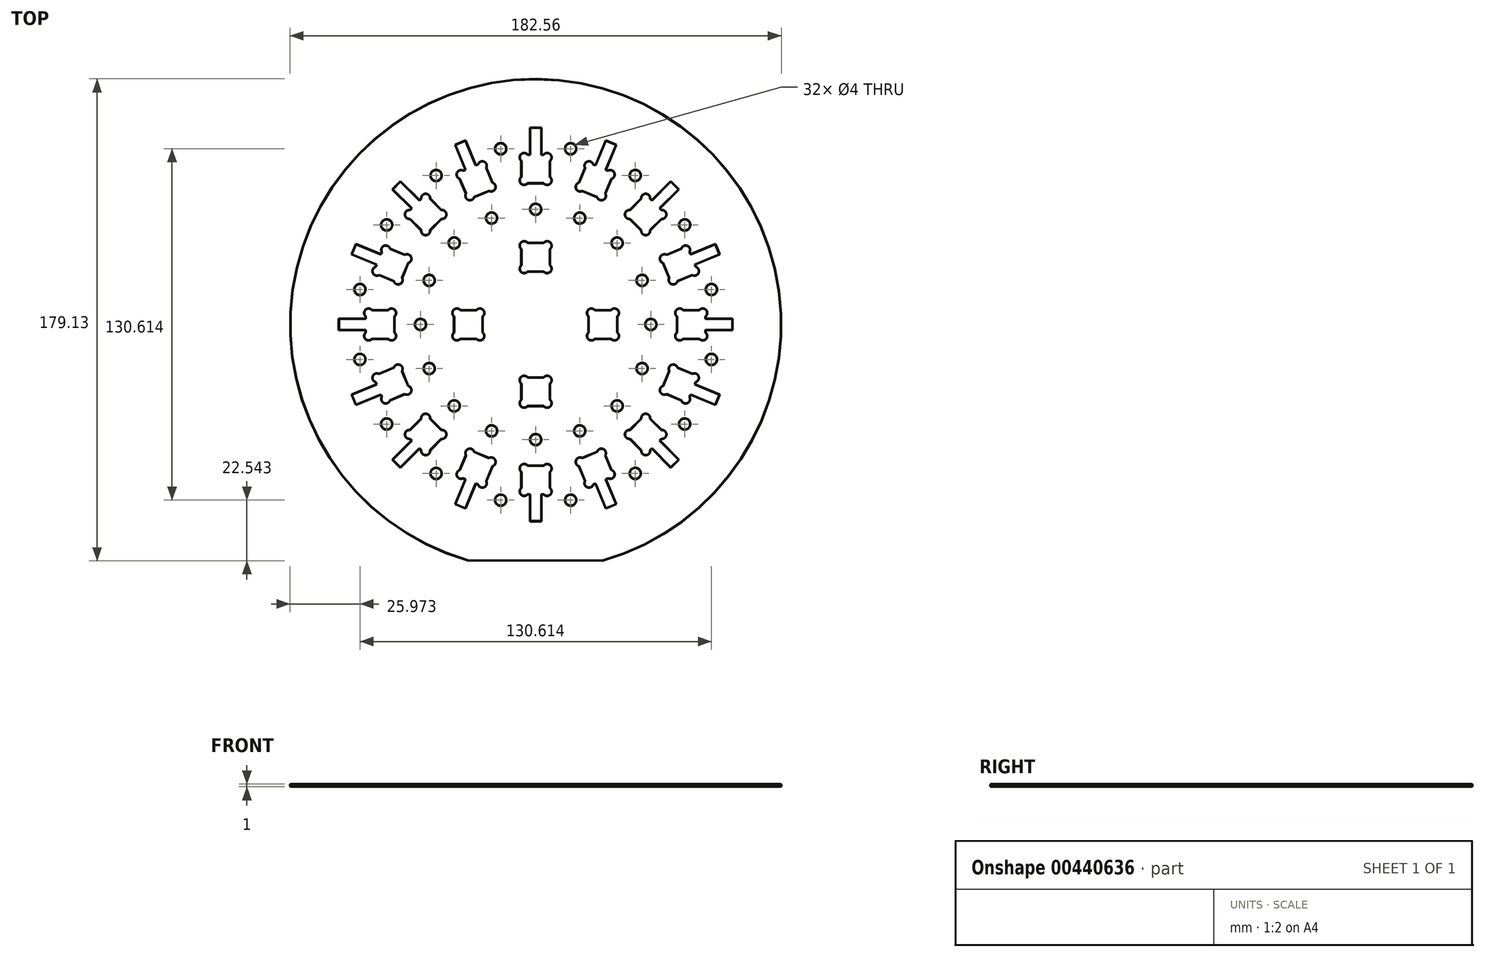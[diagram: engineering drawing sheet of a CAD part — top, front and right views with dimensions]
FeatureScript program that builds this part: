
annotation { "Feature Type Name" : "Feature", "Feature Type Description" : "" }
export const myFeature = defineFeature(function(context is Context, id is Id, definition is map)
    precondition{}
    {
        {
            var Q0;
            Q0=qCreatedBy(makeId("Top.planeOp"),FACE);
            var sketch = newSketch(context, id + "F0", { "sketchPlane" : qUnion([Q0])});
            skArc(sketch, "E0", {"start": v(24.78, -87.85) * mm, "mid": v(0.23, 91.28) * mm, "end": v(-25.22, -87.73) * mm});
            skLineSegment(sketch, "E1", {"start": v(-25.22, -87.73) * mm, "end": v(24.78, -87.85) * mm});
            skLineSegment(sketch, "E2", {"start": v(0, 0) * mm, "end": v(-0.22, -87.8) * mm, "construction": true});
            skLineSegment(sketch, "E3.bottom", {"start": v(5.25, 52.56) * mm, "end": v(3.02, 52.56) * mm, "construction": true});
            skLineSegment(sketch, "E3.top", {"start": v(5.25, 63.06) * mm, "end": v(3.02, 63.06) * mm, "construction": true});
            skLineSegment(sketch, "E3.left", {"start": v(5.25, 52.56) * mm, "end": v(5.25, 52.56) * mm});
            skLineSegment(sketch, "E3.right", {"start": v(-5.25, 52.56) * mm, "end": v(-5.25, 54.79) * mm, "construction": true});
            skPoint(sketch, "E3.middle", {"position": v(0, 57.8) * mm});
            skLineSegment(sketch, "E4", {"start": v(0, 57.8) * mm, "end": v(5.25, 63.06) * mm, "construction": true});
            skLineSegment(sketch, "E5", {"start": v(5.25, 63.06) * mm, "end": v(5.4, 63.2) * mm, "construction": true});
            skArc(sketch, "E6", {"start": v(5.25, 60.83) * mm, "mid": v(5.4, 63.2) * mm, "end": v(3.02, 63.06) * mm});
            skArc(sketch, "E7", {"start": v(3.02, 63.06) * mm, "mid": v(3.15, 60.95) * mm, "end": v(5.25, 60.83) * mm, "construction": true});
            skLineSegment(sketch, "E8", {"start": v(5.25, 60.83) * mm, "end": v(5.25, 63.06) * mm, "construction": true});
            skLineSegment(sketch, "E9", {"start": v(5.25, 52.56) * mm, "end": v(5.25, 54.79) * mm, "construction": true});
            skLineSegment(sketch, "E10", {"start": v(3.02, 63.06) * mm, "end": v(3.02, 63.06) * mm});
            skLineSegment(sketch, "E11", {"start": v(-5.25, 63.06) * mm, "end": v(-5.25, 63.06) * mm});
            skArc(sketch, "E12.1.0", {"start": v(-3.02, 63.06) * mm, "mid": v(-5.4, 63.2) * mm, "end": v(-5.25, 60.83) * mm});
            skArc(sketch, "E12.2.0", {"start": v(-5.25, 54.79) * mm, "mid": v(-5.4, 52.42) * mm, "end": v(-3.02, 52.56) * mm});
            skArc(sketch, "E13.2.3.0", {"start": v(3.02, 52.56) * mm, "mid": v(5.4, 52.42) * mm, "end": v(5.25, 54.79) * mm});
            skLineSegment(sketch, "E14", {"start": v(-5.25, 60.83) * mm, "end": v(-5.25, 63.06) * mm, "construction": true});
            skLineSegment(sketch, "E15", {"start": v(-5.25, 54.79) * mm, "end": v(-5.25, 60.83) * mm});
            skLineSegment(sketch, "E16", {"start": v(-3.02, 52.56) * mm, "end": v(-5.25, 52.56) * mm, "construction": true});
            skLineSegment(sketch, "E17", {"start": v(3.02, 52.56) * mm, "end": v(-3.02, 52.56) * mm});
            skLineSegment(sketch, "E18", {"start": v(3.02, 63.06) * mm, "end": v(-3.02, 63.06) * mm});
            skLineSegment(sketch, "E19", {"start": v(-3.02, 63.06) * mm, "end": v(-5.25, 63.06) * mm, "construction": true});
            skLineSegment(sketch, "E20", {"start": v(5.25, 54.79) * mm, "end": v(5.25, 60.83) * mm});
            skLineSegment(sketch, "E21", {"start": v(5.25, 60.83) * mm, "end": v(5.25, 60.83) * mm});
            skLineSegment(sketch, "E22", {"start": v(0, 57.8) * mm, "end": v(0, 42.8) * mm, "construction": true});
            skCircle(sketch, "E23", {"center": v(0, 42.8) * mm, "radius": 2 * mm});
            skCircle(sketch, "E24.1.0", {"center": v(13, 65.3) * mm, "radius": 2 * mm});
            skCircle(sketch, "E24.2.0", {"center": v(-13, 65.3) * mm, "radius": 2 * mm});
            skLineSegment(sketch, "E25.1.0", {"start": v(-25.82, 48.6) * mm, "end": v(-28.13, 54.19) * mm});
            skLineSegment(sketch, "E25.1.1", {"start": v(-17.32, 49.71) * mm, "end": v(-22.9, 47.4) * mm});
            skCircle(sketch, "E25.1.2", {"center": v(-16.38, 39.55) * mm, "radius": 2 * mm});
            skLineSegment(sketch, "E25.1.3", {"start": v(-22.12, 53.4) * mm, "end": v(-16.38, 39.55) * mm, "construction": true});
            skCircle(sketch, "E25.1.4", {"center": v(-37, 55.36) * mm, "radius": 2 * mm});
            skLineSegment(sketch, "E25.1.6", {"start": v(-16.12, 52.62) * mm, "end": v(-18.43, 58.2) * mm});
            skArc(sketch, "E25.1.7", {"start": v(-21.34, 59.41) * mm, "mid": v(-20.42, 57.52) * mm, "end": v(-18.43, 58.2) * mm, "construction": true});
            skPoint(sketch, "E25.1.8", {"position": v(-22.12, 53.4) * mm});
            skLineSegment(sketch, "E25.1.9", {"start": v(-22.12, 53.4) * mm, "end": v(-19.28, 60.27) * mm, "construction": true});
            skLineSegment(sketch, "E25.1.10", {"start": v(-21.34, 59.41) * mm, "end": v(-26.92, 57.1) * mm});
            skPoint(sketch, "E25.1.11", {"position": v(-22.12, 53.4) * mm});
            skArc(sketch, "E25.1.12", {"start": v(-25.82, 48.6) * mm, "mid": v(-25.04, 46.36) * mm, "end": v(-22.9, 47.4) * mm});
            skPoint(sketch, "E25.1.13", {"position": v(-22.12, 53.4) * mm});
            skLineSegment(sketch, "E25.1.14", {"start": v(-24.96, 46.55) * mm, "end": v(-25.82, 48.6) * mm, "construction": true});
            skLineSegment(sketch, "E25.1.15", {"start": v(-26.92, 57.1) * mm, "end": v(-28.98, 56.25) * mm, "construction": true});
            skArc(sketch, "E25.1.16", {"start": v(-26.92, 57.1) * mm, "mid": v(-29.17, 56.32) * mm, "end": v(-28.13, 54.19) * mm});
            skLineSegment(sketch, "E25.1.17", {"start": v(-15.26, 50.57) * mm, "end": v(-16.12, 52.62) * mm, "construction": true});
            skPoint(sketch, "E25.1.18", {"position": v(-22.12, 53.4) * mm});
            skLineSegment(sketch, "E25.1.19", {"start": v(-22.9, 47.4) * mm, "end": v(-24.96, 46.55) * mm, "construction": true});
            skArc(sketch, "E25.1.20", {"start": v(-17.32, 49.71) * mm, "mid": v(-15.08, 50.49) * mm, "end": v(-16.12, 52.62) * mm});
            skLineSegment(sketch, "E25.1.21", {"start": v(-15.26, 50.57) * mm, "end": v(-17.32, 49.71) * mm, "construction": true});
            skLineSegment(sketch, "E25.1.22", {"start": v(-28.13, 54.19) * mm, "end": v(-28.98, 56.25) * mm, "construction": true});
            skPoint(sketch, "E25.1.23", {"position": v(-22.12, 53.4) * mm});
            skPoint(sketch, "E25.1.24", {"position": v(-22.12, 53.4) * mm});
            skLineSegment(sketch, "E25.1.25", {"start": v(-18.43, 58.2) * mm, "end": v(-19.28, 60.27) * mm, "construction": true});
            skArc(sketch, "E25.1.26", {"start": v(-18.43, 58.2) * mm, "mid": v(-19.2, 60.45) * mm, "end": v(-21.34, 59.41) * mm});
            skLineSegment(sketch, "E25.1.27", {"start": v(-19.28, 60.27) * mm, "end": v(-19.2, 60.45) * mm, "construction": true});
            skLineSegment(sketch, "E25.1.28", {"start": v(-19.28, 60.27) * mm, "end": v(-21.34, 59.41) * mm, "construction": true});
            skLineSegment(sketch, "E25.2.0", {"start": v(-42.45, 35.03) * mm, "end": v(-46.72, 39.3) * mm});
            skLineSegment(sketch, "E25.2.1", {"start": v(-35.03, 39.3) * mm, "end": v(-39.3, 35.03) * mm});
            skCircle(sketch, "E25.2.2", {"center": v(-30.27, 30.27) * mm, "radius": 2 * mm});
            skLineSegment(sketch, "E25.2.3", {"start": v(-40.88, 40.88) * mm, "end": v(-30.27, 30.27) * mm, "construction": true});
            skCircle(sketch, "E25.2.4", {"center": v(-55.36, 37) * mm, "radius": 2 * mm});
            skCircle(sketch, "E25.2.5", {"center": v(-37, 55.36) * mm, "radius": 2 * mm});
            skLineSegment(sketch, "E25.2.6", {"start": v(-35.03, 42.45) * mm, "end": v(-39.3, 46.72) * mm});
            skArc(sketch, "E25.2.7", {"start": v(-42.45, 46.72) * mm, "mid": v(-40.88, 45.33) * mm, "end": v(-39.3, 46.72) * mm, "construction": true});
            skPoint(sketch, "E25.2.8", {"position": v(-40.88, 40.88) * mm});
            skLineSegment(sketch, "E25.2.9", {"start": v(-40.88, 40.88) * mm, "end": v(-40.88, 48.3) * mm, "construction": true});
            skLineSegment(sketch, "E25.2.10", {"start": v(-42.45, 46.72) * mm, "end": v(-46.72, 42.45) * mm});
            skPoint(sketch, "E25.2.11", {"position": v(-40.88, 40.88) * mm});
            skArc(sketch, "E25.2.12", {"start": v(-42.45, 35.03) * mm, "mid": v(-40.88, 33.25) * mm, "end": v(-39.3, 35.03) * mm});
            skPoint(sketch, "E25.2.13", {"position": v(-40.88, 40.88) * mm});
            skLineSegment(sketch, "E25.2.14", {"start": v(-40.88, 33.45) * mm, "end": v(-42.45, 35.03) * mm, "construction": true});
            skLineSegment(sketch, "E25.2.15", {"start": v(-46.72, 42.45) * mm, "end": v(-48.3, 40.88) * mm, "construction": true});
            skArc(sketch, "E25.2.16", {"start": v(-46.72, 42.45) * mm, "mid": v(-48.5, 40.88) * mm, "end": v(-46.72, 39.3) * mm});
            skLineSegment(sketch, "E25.2.17", {"start": v(-33.45, 40.88) * mm, "end": v(-35.03, 42.45) * mm, "construction": true});
            skPoint(sketch, "E25.2.18", {"position": v(-40.88, 40.88) * mm});
            skLineSegment(sketch, "E25.2.19", {"start": v(-39.3, 35.03) * mm, "end": v(-40.88, 33.45) * mm, "construction": true});
            skArc(sketch, "E25.2.20", {"start": v(-35.03, 39.3) * mm, "mid": v(-33.25, 40.88) * mm, "end": v(-35.03, 42.45) * mm});
            skLineSegment(sketch, "E25.2.21", {"start": v(-33.45, 40.88) * mm, "end": v(-35.03, 39.3) * mm, "construction": true});
            skLineSegment(sketch, "E25.2.22", {"start": v(-46.72, 39.3) * mm, "end": v(-48.3, 40.88) * mm, "construction": true});
            skPoint(sketch, "E25.2.23", {"position": v(-40.88, 40.88) * mm});
            skPoint(sketch, "E25.2.24", {"position": v(-40.88, 40.88) * mm});
            skLineSegment(sketch, "E25.2.25", {"start": v(-39.3, 46.72) * mm, "end": v(-40.88, 48.3) * mm, "construction": true});
            skArc(sketch, "E25.2.26", {"start": v(-39.3, 46.72) * mm, "mid": v(-40.88, 48.5) * mm, "end": v(-42.45, 46.72) * mm});
            skLineSegment(sketch, "E25.2.27", {"start": v(-40.88, 48.3) * mm, "end": v(-40.88, 48.5) * mm, "construction": true});
            skLineSegment(sketch, "E25.2.28", {"start": v(-40.88, 48.3) * mm, "end": v(-42.45, 46.72) * mm, "construction": true});
            skLineSegment(sketch, "E26.3.3.0", {"start": v(-47.4, 22.9) * mm, "end": v(-49.71, 17.32) * mm});
            skCircle(sketch, "E26.6.3.0", {"center": v(-39.55, 16.38) * mm, "radius": 2 * mm});
            skLineSegment(sketch, "E26.7.3.0", {"start": v(-52.62, 16.12) * mm, "end": v(-58.2, 18.43) * mm});
            skLineSegment(sketch, "E26.8.3.0", {"start": v(-53.4, 22.12) * mm, "end": v(-39.55, 16.38) * mm, "construction": true});
            skCircle(sketch, "E26.11.3.0", {"center": v(-65.3, 13) * mm, "radius": 2 * mm});
            skLineSegment(sketch, "E26.15.3.0", {"start": v(-48.6, 25.82) * mm, "end": v(-54.19, 28.13) * mm});
            skArc(sketch, "E26.18.3.0", {"start": v(-57.1, 26.92) * mm, "mid": v(-55.1, 26.23) * mm, "end": v(-54.19, 28.13) * mm, "construction": true});
            skPoint(sketch, "E26.22.3.0", {"position": v(-53.4, 22.12) * mm});
            skLineSegment(sketch, "E26.23.3.0", {"start": v(-53.4, 22.12) * mm, "end": v(-56.25, 28.98) * mm, "construction": true});
            skLineSegment(sketch, "E26.26.3.0", {"start": v(-57.1, 26.92) * mm, "end": v(-59.41, 21.34) * mm});
            skPoint(sketch, "E26.29.3.0", {"position": v(-53.4, 22.12) * mm});
            skArc(sketch, "E26.30.3.0", {"start": v(-52.62, 16.12) * mm, "mid": v(-50.49, 15.08) * mm, "end": v(-49.71, 17.32) * mm});
            skPoint(sketch, "E26.34.3.0", {"position": v(-53.4, 22.12) * mm});
            skLineSegment(sketch, "E26.35.3.0", {"start": v(-50.57, 15.26) * mm, "end": v(-52.62, 16.12) * mm, "construction": true});
            skLineSegment(sketch, "E26.38.3.0", {"start": v(-59.41, 21.34) * mm, "end": v(-60.27, 19.28) * mm, "construction": true});
            skArc(sketch, "E26.41.3.0", {"start": v(-59.41, 21.34) * mm, "mid": v(-60.45, 19.2) * mm, "end": v(-58.2, 18.43) * mm});
            skLineSegment(sketch, "E26.45.3.0", {"start": v(-46.55, 24.96) * mm, "end": v(-48.6, 25.82) * mm, "construction": true});
            skPoint(sketch, "E26.48.3.0", {"position": v(-53.4, 22.12) * mm});
            skLineSegment(sketch, "E26.49.3.0", {"start": v(-49.71, 17.32) * mm, "end": v(-50.57, 15.26) * mm, "construction": true});
            skArc(sketch, "E26.52.3.0", {"start": v(-47.4, 22.9) * mm, "mid": v(-46.36, 25.04) * mm, "end": v(-48.6, 25.82) * mm});
            skLineSegment(sketch, "E26.56.3.0", {"start": v(-46.55, 24.96) * mm, "end": v(-47.4, 22.9) * mm, "construction": true});
            skLineSegment(sketch, "E26.59.3.0", {"start": v(-58.2, 18.43) * mm, "end": v(-60.27, 19.28) * mm, "construction": true});
            skPoint(sketch, "E26.62.3.0", {"position": v(-53.4, 22.12) * mm});
            skPoint(sketch, "E26.63.3.0", {"position": v(-53.4, 22.12) * mm});
            skLineSegment(sketch, "E26.64.3.0", {"start": v(-54.19, 28.13) * mm, "end": v(-56.25, 28.98) * mm, "construction": true});
            skArc(sketch, "E26.67.3.0", {"start": v(-54.19, 28.13) * mm, "mid": v(-56.32, 29.17) * mm, "end": v(-57.1, 26.92) * mm});
            skLineSegment(sketch, "E26.71.3.0", {"start": v(-56.25, 28.98) * mm, "end": v(-56.32, 29.17) * mm, "construction": true});
            skLineSegment(sketch, "E26.74.3.0", {"start": v(-56.25, 28.98) * mm, "end": v(-57.1, 26.92) * mm, "construction": true});
            skLineSegment(sketch, "E26.3.4.0", {"start": v(-52.56, 3.02) * mm, "end": v(-52.56, -3.02) * mm});
            skCircle(sketch, "E26.6.4.0", {"center": v(-42.8, 0) * mm, "radius": 2 * mm});
            skLineSegment(sketch, "E26.7.4.0", {"start": v(-54.79, -5.25) * mm, "end": v(-60.83, -5.25) * mm});
            skLineSegment(sketch, "E26.8.4.0", {"start": v(-57.8, 0) * mm, "end": v(-42.8, 0) * mm, "construction": true});
            skCircle(sketch, "E26.11.4.0", {"center": v(-65.3, -13) * mm, "radius": 2 * mm});
            skCircle(sketch, "E26.13.4.0", {"center": v(-65.3, 13) * mm, "radius": 2 * mm});
            skLineSegment(sketch, "E26.15.4.0", {"start": v(-54.79, 5.25) * mm, "end": v(-60.83, 5.25) * mm});
            skArc(sketch, "E26.18.4.0", {"start": v(-63.06, 3.02) * mm, "mid": v(-60.95, 3.15) * mm, "end": v(-60.83, 5.25) * mm, "construction": true});
            skPoint(sketch, "E26.22.4.0", {"position": v(-57.8, 0) * mm});
            skLineSegment(sketch, "E26.23.4.0", {"start": v(-57.8, 0) * mm, "end": v(-63.06, 5.25) * mm, "construction": true});
            skLineSegment(sketch, "E26.26.4.0", {"start": v(-63.06, 3.02) * mm, "end": v(-63.06, -3.02) * mm});
            skPoint(sketch, "E26.29.4.0", {"position": v(-57.8, 0) * mm});
            skArc(sketch, "E26.30.4.0", {"start": v(-54.79, -5.25) * mm, "mid": v(-52.42, -5.4) * mm, "end": v(-52.56, -3.02) * mm});
            skPoint(sketch, "E26.34.4.0", {"position": v(-57.8, 0) * mm});
            skLineSegment(sketch, "E26.35.4.0", {"start": v(-52.56, -5.25) * mm, "end": v(-54.79, -5.25) * mm, "construction": true});
            skLineSegment(sketch, "E26.38.4.0", {"start": v(-63.06, -3.02) * mm, "end": v(-63.06, -5.25) * mm, "construction": true});
            skArc(sketch, "E26.41.4.0", {"start": v(-63.06, -3.02) * mm, "mid": v(-63.2, -5.4) * mm, "end": v(-60.83, -5.25) * mm});
            skLineSegment(sketch, "E26.45.4.0", {"start": v(-52.56, 5.25) * mm, "end": v(-54.79, 5.25) * mm, "construction": true});
            skPoint(sketch, "E26.48.4.0", {"position": v(-57.8, 0) * mm});
            skLineSegment(sketch, "E26.49.4.0", {"start": v(-52.56, -3.02) * mm, "end": v(-52.56, -5.25) * mm, "construction": true});
            skArc(sketch, "E26.52.4.0", {"start": v(-52.56, 3.02) * mm, "mid": v(-52.42, 5.4) * mm, "end": v(-54.79, 5.25) * mm});
            skLineSegment(sketch, "E26.56.4.0", {"start": v(-52.56, 5.25) * mm, "end": v(-52.56, 3.02) * mm, "construction": true});
            skLineSegment(sketch, "E26.59.4.0", {"start": v(-60.83, -5.25) * mm, "end": v(-63.06, -5.25) * mm, "construction": true});
            skPoint(sketch, "E26.62.4.0", {"position": v(-57.8, 0) * mm});
            skPoint(sketch, "E26.63.4.0", {"position": v(-57.8, 0) * mm});
            skLineSegment(sketch, "E26.64.4.0", {"start": v(-60.83, 5.25) * mm, "end": v(-63.06, 5.25) * mm, "construction": true});
            skArc(sketch, "E26.67.4.0", {"start": v(-60.83, 5.25) * mm, "mid": v(-63.2, 5.4) * mm, "end": v(-63.06, 3.02) * mm});
            skLineSegment(sketch, "E26.71.4.0", {"start": v(-63.06, 5.25) * mm, "end": v(-63.2, 5.4) * mm, "construction": true});
            skLineSegment(sketch, "E26.74.4.0", {"start": v(-63.06, 5.25) * mm, "end": v(-63.06, 3.02) * mm, "construction": true});
            skLineSegment(sketch, "E27.3.5.0", {"start": v(-49.71, -17.32) * mm, "end": v(-47.4, -22.9) * mm});
            skCircle(sketch, "E27.6.5.0", {"center": v(-39.55, -16.38) * mm, "radius": 2 * mm});
            skLineSegment(sketch, "E27.7.5.0", {"start": v(-48.6, -25.82) * mm, "end": v(-54.19, -28.13) * mm});
            skLineSegment(sketch, "E27.8.5.0", {"start": v(-53.4, -22.12) * mm, "end": v(-39.55, -16.38) * mm, "construction": true});
            skCircle(sketch, "E27.11.5.0", {"center": v(-55.36, -37) * mm, "radius": 2 * mm});
            skLineSegment(sketch, "E27.15.5.0", {"start": v(-52.62, -16.12) * mm, "end": v(-58.2, -18.43) * mm});
            skArc(sketch, "E27.18.5.0", {"start": v(-59.41, -21.34) * mm, "mid": v(-57.52, -20.42) * mm, "end": v(-58.2, -18.43) * mm, "construction": true});
            skPoint(sketch, "E27.22.5.0", {"position": v(-53.4, -22.12) * mm});
            skLineSegment(sketch, "E27.23.5.0", {"start": v(-53.4, -22.12) * mm, "end": v(-60.27, -19.28) * mm, "construction": true});
            skLineSegment(sketch, "E27.26.5.0", {"start": v(-59.41, -21.34) * mm, "end": v(-57.1, -26.92) * mm});
            skPoint(sketch, "E27.29.5.0", {"position": v(-53.4, -22.12) * mm});
            skArc(sketch, "E27.30.5.0", {"start": v(-48.6, -25.82) * mm, "mid": v(-46.36, -25.04) * mm, "end": v(-47.4, -22.9) * mm});
            skPoint(sketch, "E27.34.5.0", {"position": v(-53.4, -22.12) * mm});
            skLineSegment(sketch, "E27.35.5.0", {"start": v(-46.55, -24.96) * mm, "end": v(-48.6, -25.82) * mm, "construction": true});
            skLineSegment(sketch, "E27.38.5.0", {"start": v(-57.1, -26.92) * mm, "end": v(-56.25, -28.98) * mm, "construction": true});
            skArc(sketch, "E27.41.5.0", {"start": v(-57.1, -26.92) * mm, "mid": v(-56.32, -29.17) * mm, "end": v(-54.19, -28.13) * mm});
            skLineSegment(sketch, "E27.45.5.0", {"start": v(-50.57, -15.26) * mm, "end": v(-52.62, -16.12) * mm, "construction": true});
            skPoint(sketch, "E27.48.5.0", {"position": v(-53.4, -22.12) * mm});
            skLineSegment(sketch, "E27.49.5.0", {"start": v(-47.4, -22.9) * mm, "end": v(-46.55, -24.96) * mm, "construction": true});
            skArc(sketch, "E27.52.5.0", {"start": v(-49.71, -17.32) * mm, "mid": v(-50.49, -15.08) * mm, "end": v(-52.62, -16.12) * mm});
            skLineSegment(sketch, "E27.56.5.0", {"start": v(-50.57, -15.26) * mm, "end": v(-49.71, -17.32) * mm, "construction": true});
            skLineSegment(sketch, "E27.59.5.0", {"start": v(-54.19, -28.13) * mm, "end": v(-56.25, -28.98) * mm, "construction": true});
            skPoint(sketch, "E27.62.5.0", {"position": v(-53.4, -22.12) * mm});
            skPoint(sketch, "E27.63.5.0", {"position": v(-53.4, -22.12) * mm});
            skLineSegment(sketch, "E27.64.5.0", {"start": v(-58.2, -18.43) * mm, "end": v(-60.27, -19.28) * mm, "construction": true});
            skArc(sketch, "E27.67.5.0", {"start": v(-58.2, -18.43) * mm, "mid": v(-60.45, -19.2) * mm, "end": v(-59.41, -21.34) * mm});
            skLineSegment(sketch, "E27.71.5.0", {"start": v(-60.27, -19.28) * mm, "end": v(-60.45, -19.2) * mm, "construction": true});
            skLineSegment(sketch, "E27.74.5.0", {"start": v(-60.27, -19.28) * mm, "end": v(-59.41, -21.34) * mm, "construction": true});
            skLineSegment(sketch, "E27.3.6.0", {"start": v(-39.3, -35.03) * mm, "end": v(-35.03, -39.3) * mm});
            skCircle(sketch, "E27.6.6.0", {"center": v(-30.27, -30.27) * mm, "radius": 2 * mm});
            skLineSegment(sketch, "E27.7.6.0", {"start": v(-35.03, -42.45) * mm, "end": v(-39.3, -46.72) * mm});
            skLineSegment(sketch, "E27.8.6.0", {"start": v(-40.88, -40.88) * mm, "end": v(-30.27, -30.27) * mm, "construction": true});
            skCircle(sketch, "E27.11.6.0", {"center": v(-37, -55.36) * mm, "radius": 2 * mm});
            skCircle(sketch, "E27.13.6.0", {"center": v(-55.36, -37) * mm, "radius": 2 * mm});
            skLineSegment(sketch, "E27.15.6.0", {"start": v(-42.45, -35.03) * mm, "end": v(-46.72, -39.3) * mm});
            skArc(sketch, "E27.18.6.0", {"start": v(-46.72, -42.45) * mm, "mid": v(-45.33, -40.88) * mm, "end": v(-46.72, -39.3) * mm, "construction": true});
            skPoint(sketch, "E27.22.6.0", {"position": v(-40.88, -40.88) * mm});
            skLineSegment(sketch, "E27.23.6.0", {"start": v(-40.88, -40.88) * mm, "end": v(-48.3, -40.88) * mm, "construction": true});
            skLineSegment(sketch, "E27.26.6.0", {"start": v(-46.72, -42.45) * mm, "end": v(-42.45, -46.72) * mm});
            skPoint(sketch, "E27.29.6.0", {"position": v(-40.88, -40.88) * mm});
            skArc(sketch, "E27.30.6.0", {"start": v(-35.03, -42.45) * mm, "mid": v(-33.25, -40.88) * mm, "end": v(-35.03, -39.3) * mm});
            skPoint(sketch, "E27.34.6.0", {"position": v(-40.88, -40.88) * mm});
            skLineSegment(sketch, "E27.35.6.0", {"start": v(-33.45, -40.88) * mm, "end": v(-35.03, -42.45) * mm, "construction": true});
            skLineSegment(sketch, "E27.38.6.0", {"start": v(-42.45, -46.72) * mm, "end": v(-40.88, -48.3) * mm, "construction": true});
            skArc(sketch, "E27.41.6.0", {"start": v(-42.45, -46.72) * mm, "mid": v(-40.88, -48.5) * mm, "end": v(-39.3, -46.72) * mm});
            skLineSegment(sketch, "E27.45.6.0", {"start": v(-40.88, -33.45) * mm, "end": v(-42.45, -35.03) * mm, "construction": true});
            skPoint(sketch, "E27.48.6.0", {"position": v(-40.88, -40.88) * mm});
            skLineSegment(sketch, "E27.49.6.0", {"start": v(-35.03, -39.3) * mm, "end": v(-33.45, -40.88) * mm, "construction": true});
            skArc(sketch, "E27.52.6.0", {"start": v(-39.3, -35.03) * mm, "mid": v(-40.88, -33.25) * mm, "end": v(-42.45, -35.03) * mm});
            skLineSegment(sketch, "E27.56.6.0", {"start": v(-40.88, -33.45) * mm, "end": v(-39.3, -35.03) * mm, "construction": true});
            skLineSegment(sketch, "E27.59.6.0", {"start": v(-39.3, -46.72) * mm, "end": v(-40.88, -48.3) * mm, "construction": true});
            skPoint(sketch, "E27.62.6.0", {"position": v(-40.88, -40.88) * mm});
            skPoint(sketch, "E27.63.6.0", {"position": v(-40.88, -40.88) * mm});
            skLineSegment(sketch, "E27.64.6.0", {"start": v(-46.72, -39.3) * mm, "end": v(-48.3, -40.88) * mm, "construction": true});
            skArc(sketch, "E27.67.6.0", {"start": v(-46.72, -39.3) * mm, "mid": v(-48.5, -40.88) * mm, "end": v(-46.72, -42.45) * mm});
            skLineSegment(sketch, "E27.71.6.0", {"start": v(-48.3, -40.88) * mm, "end": v(-48.5, -40.88) * mm, "construction": true});
            skLineSegment(sketch, "E27.74.6.0", {"start": v(-48.3, -40.88) * mm, "end": v(-46.72, -42.45) * mm, "construction": true});
            skLineSegment(sketch, "E27.3.7.0", {"start": v(-22.9, -47.4) * mm, "end": v(-17.32, -49.71) * mm});
            skCircle(sketch, "E27.6.7.0", {"center": v(-16.38, -39.55) * mm, "radius": 2 * mm});
            skLineSegment(sketch, "E27.7.7.0", {"start": v(-16.12, -52.62) * mm, "end": v(-18.43, -58.2) * mm});
            skLineSegment(sketch, "E27.8.7.0", {"start": v(-22.12, -53.4) * mm, "end": v(-16.38, -39.55) * mm, "construction": true});
            skCircle(sketch, "E27.11.7.0", {"center": v(-13, -65.3) * mm, "radius": 2 * mm});
            skCircle(sketch, "E27.13.7.0", {"center": v(-37, -55.36) * mm, "radius": 2 * mm});
            skLineSegment(sketch, "E27.15.7.0", {"start": v(-25.82, -48.6) * mm, "end": v(-28.13, -54.19) * mm});
            skArc(sketch, "E27.18.7.0", {"start": v(-26.92, -57.1) * mm, "mid": v(-26.23, -55.1) * mm, "end": v(-28.13, -54.19) * mm, "construction": true});
            skPoint(sketch, "E27.22.7.0", {"position": v(-22.12, -53.4) * mm});
            skLineSegment(sketch, "E27.23.7.0", {"start": v(-22.12, -53.4) * mm, "end": v(-28.98, -56.25) * mm, "construction": true});
            skLineSegment(sketch, "E27.26.7.0", {"start": v(-26.92, -57.1) * mm, "end": v(-21.34, -59.41) * mm});
            skPoint(sketch, "E27.29.7.0", {"position": v(-22.12, -53.4) * mm});
            skArc(sketch, "E27.30.7.0", {"start": v(-16.12, -52.62) * mm, "mid": v(-15.08, -50.49) * mm, "end": v(-17.32, -49.71) * mm});
            skPoint(sketch, "E27.34.7.0", {"position": v(-22.12, -53.4) * mm});
            skLineSegment(sketch, "E27.35.7.0", {"start": v(-15.26, -50.57) * mm, "end": v(-16.12, -52.62) * mm, "construction": true});
            skLineSegment(sketch, "E27.38.7.0", {"start": v(-21.34, -59.41) * mm, "end": v(-19.28, -60.27) * mm, "construction": true});
            skArc(sketch, "E27.41.7.0", {"start": v(-21.34, -59.41) * mm, "mid": v(-19.2, -60.45) * mm, "end": v(-18.43, -58.2) * mm});
            skLineSegment(sketch, "E27.45.7.0", {"start": v(-24.96, -46.55) * mm, "end": v(-25.82, -48.6) * mm, "construction": true});
            skPoint(sketch, "E27.48.7.0", {"position": v(-22.12, -53.4) * mm});
            skLineSegment(sketch, "E27.49.7.0", {"start": v(-17.32, -49.71) * mm, "end": v(-15.26, -50.57) * mm, "construction": true});
            skArc(sketch, "E27.52.7.0", {"start": v(-22.9, -47.4) * mm, "mid": v(-25.04, -46.36) * mm, "end": v(-25.82, -48.6) * mm});
            skLineSegment(sketch, "E27.56.7.0", {"start": v(-24.96, -46.55) * mm, "end": v(-22.9, -47.4) * mm, "construction": true});
            skLineSegment(sketch, "E27.59.7.0", {"start": v(-18.43, -58.2) * mm, "end": v(-19.28, -60.27) * mm, "construction": true});
            skPoint(sketch, "E27.62.7.0", {"position": v(-22.12, -53.4) * mm});
            skPoint(sketch, "E27.63.7.0", {"position": v(-22.12, -53.4) * mm});
            skLineSegment(sketch, "E27.64.7.0", {"start": v(-28.13, -54.19) * mm, "end": v(-28.98, -56.25) * mm, "construction": true});
            skArc(sketch, "E27.67.7.0", {"start": v(-28.13, -54.19) * mm, "mid": v(-29.17, -56.32) * mm, "end": v(-26.92, -57.1) * mm});
            skLineSegment(sketch, "E27.71.7.0", {"start": v(-28.98, -56.25) * mm, "end": v(-29.17, -56.32) * mm, "construction": true});
            skLineSegment(sketch, "E27.74.7.0", {"start": v(-28.98, -56.25) * mm, "end": v(-26.92, -57.1) * mm, "construction": true});
            skLineSegment(sketch, "E27.3.8.0", {"start": v(-3.02, -52.56) * mm, "end": v(3.02, -52.56) * mm});
            skCircle(sketch, "E27.6.8.0", {"center": v(0, -42.8) * mm, "radius": 2 * mm});
            skLineSegment(sketch, "E27.7.8.0", {"start": v(5.25, -54.79) * mm, "end": v(5.25, -60.83) * mm});
            skLineSegment(sketch, "E27.8.8.0", {"start": v(0, -57.8) * mm, "end": v(0, -42.8) * mm, "construction": true});
            skCircle(sketch, "E27.11.8.0", {"center": v(13, -65.3) * mm, "radius": 2 * mm});
            skCircle(sketch, "E27.13.8.0", {"center": v(-13, -65.3) * mm, "radius": 2 * mm});
            skLineSegment(sketch, "E27.15.8.0", {"start": v(-5.25, -54.79) * mm, "end": v(-5.25, -60.83) * mm});
            skArc(sketch, "E27.18.8.0", {"start": v(-3.02, -63.06) * mm, "mid": v(-3.15, -60.95) * mm, "end": v(-5.25, -60.83) * mm, "construction": true});
            skPoint(sketch, "E27.22.8.0", {"position": v(0, -57.8) * mm});
            skLineSegment(sketch, "E27.23.8.0", {"start": v(0, -57.8) * mm, "end": v(-5.25, -63.06) * mm, "construction": true});
            skLineSegment(sketch, "E27.26.8.0", {"start": v(-3.02, -63.06) * mm, "end": v(3.02, -63.06) * mm});
            skPoint(sketch, "E27.29.8.0", {"position": v(0, -57.8) * mm});
            skArc(sketch, "E27.30.8.0", {"start": v(5.25, -54.79) * mm, "mid": v(5.4, -52.42) * mm, "end": v(3.02, -52.56) * mm});
            skPoint(sketch, "E27.34.8.0", {"position": v(0, -57.8) * mm});
            skLineSegment(sketch, "E27.35.8.0", {"start": v(5.25, -52.56) * mm, "end": v(5.25, -54.79) * mm, "construction": true});
            skLineSegment(sketch, "E27.38.8.0", {"start": v(3.02, -63.06) * mm, "end": v(5.25, -63.06) * mm, "construction": true});
            skArc(sketch, "E27.41.8.0", {"start": v(3.02, -63.06) * mm, "mid": v(5.4, -63.2) * mm, "end": v(5.25, -60.83) * mm});
            skLineSegment(sketch, "E27.45.8.0", {"start": v(-5.25, -52.56) * mm, "end": v(-5.25, -54.79) * mm, "construction": true});
            skPoint(sketch, "E27.48.8.0", {"position": v(0, -57.8) * mm});
            skLineSegment(sketch, "E27.49.8.0", {"start": v(3.02, -52.56) * mm, "end": v(5.25, -52.56) * mm, "construction": true});
            skArc(sketch, "E27.52.8.0", {"start": v(-3.02, -52.56) * mm, "mid": v(-5.4, -52.42) * mm, "end": v(-5.25, -54.79) * mm});
            skLineSegment(sketch, "E27.56.8.0", {"start": v(-5.25, -52.56) * mm, "end": v(-3.02, -52.56) * mm, "construction": true});
            skLineSegment(sketch, "E27.59.8.0", {"start": v(5.25, -60.83) * mm, "end": v(5.25, -63.06) * mm, "construction": true});
            skPoint(sketch, "E27.62.8.0", {"position": v(0, -57.8) * mm});
            skPoint(sketch, "E27.63.8.0", {"position": v(0, -57.8) * mm});
            skLineSegment(sketch, "E27.64.8.0", {"start": v(-5.25, -60.83) * mm, "end": v(-5.25, -63.06) * mm, "construction": true});
            skArc(sketch, "E27.67.8.0", {"start": v(-5.25, -60.83) * mm, "mid": v(-5.4, -63.2) * mm, "end": v(-3.02, -63.06) * mm});
            skLineSegment(sketch, "E27.71.8.0", {"start": v(-5.25, -63.06) * mm, "end": v(-5.4, -63.2) * mm, "construction": true});
            skLineSegment(sketch, "E27.74.8.0", {"start": v(-5.25, -63.06) * mm, "end": v(-3.02, -63.06) * mm, "construction": true});
            skLineSegment(sketch, "E27.3.9.0", {"start": v(17.32, -49.71) * mm, "end": v(22.9, -47.4) * mm});
            skCircle(sketch, "E27.6.9.0", {"center": v(16.38, -39.55) * mm, "radius": 2 * mm});
            skLineSegment(sketch, "E27.7.9.0", {"start": v(25.82, -48.6) * mm, "end": v(28.13, -54.19) * mm});
            skLineSegment(sketch, "E27.8.9.0", {"start": v(22.12, -53.4) * mm, "end": v(16.38, -39.55) * mm, "construction": true});
            skCircle(sketch, "E27.11.9.0", {"center": v(37, -55.36) * mm, "radius": 2 * mm});
            skCircle(sketch, "E27.13.9.0", {"center": v(13, -65.3) * mm, "radius": 2 * mm});
            skLineSegment(sketch, "E27.15.9.0", {"start": v(16.12, -52.62) * mm, "end": v(18.43, -58.2) * mm});
            skArc(sketch, "E27.18.9.0", {"start": v(21.34, -59.41) * mm, "mid": v(20.42, -57.52) * mm, "end": v(18.43, -58.2) * mm, "construction": true});
            skPoint(sketch, "E27.22.9.0", {"position": v(22.12, -53.4) * mm});
            skLineSegment(sketch, "E27.23.9.0", {"start": v(22.12, -53.4) * mm, "end": v(19.28, -60.27) * mm, "construction": true});
            skLineSegment(sketch, "E27.26.9.0", {"start": v(21.34, -59.41) * mm, "end": v(26.92, -57.1) * mm});
            skPoint(sketch, "E27.29.9.0", {"position": v(22.12, -53.4) * mm});
            skArc(sketch, "E27.30.9.0", {"start": v(25.82, -48.6) * mm, "mid": v(25.04, -46.36) * mm, "end": v(22.9, -47.4) * mm});
            skPoint(sketch, "E27.34.9.0", {"position": v(22.12, -53.4) * mm});
            skLineSegment(sketch, "E27.35.9.0", {"start": v(24.96, -46.55) * mm, "end": v(25.82, -48.6) * mm, "construction": true});
            skLineSegment(sketch, "E27.38.9.0", {"start": v(26.92, -57.1) * mm, "end": v(28.98, -56.25) * mm, "construction": true});
            skArc(sketch, "E27.41.9.0", {"start": v(26.92, -57.1) * mm, "mid": v(29.17, -56.32) * mm, "end": v(28.13, -54.19) * mm});
            skLineSegment(sketch, "E27.45.9.0", {"start": v(15.26, -50.57) * mm, "end": v(16.12, -52.62) * mm, "construction": true});
            skPoint(sketch, "E27.48.9.0", {"position": v(22.12, -53.4) * mm});
            skLineSegment(sketch, "E27.49.9.0", {"start": v(22.9, -47.4) * mm, "end": v(24.96, -46.55) * mm, "construction": true});
            skArc(sketch, "E27.52.9.0", {"start": v(17.32, -49.71) * mm, "mid": v(15.08, -50.49) * mm, "end": v(16.12, -52.62) * mm});
            skLineSegment(sketch, "E27.56.9.0", {"start": v(15.26, -50.57) * mm, "end": v(17.32, -49.71) * mm, "construction": true});
            skLineSegment(sketch, "E27.59.9.0", {"start": v(28.13, -54.19) * mm, "end": v(28.98, -56.25) * mm, "construction": true});
            skPoint(sketch, "E27.62.9.0", {"position": v(22.12, -53.4) * mm});
            skPoint(sketch, "E27.63.9.0", {"position": v(22.12, -53.4) * mm});
            skLineSegment(sketch, "E27.64.9.0", {"start": v(18.43, -58.2) * mm, "end": v(19.28, -60.27) * mm, "construction": true});
            skArc(sketch, "E27.67.9.0", {"start": v(18.43, -58.2) * mm, "mid": v(19.2, -60.45) * mm, "end": v(21.34, -59.41) * mm});
            skLineSegment(sketch, "E27.71.9.0", {"start": v(19.28, -60.27) * mm, "end": v(19.2, -60.45) * mm, "construction": true});
            skLineSegment(sketch, "E27.74.9.0", {"start": v(19.28, -60.27) * mm, "end": v(21.34, -59.41) * mm, "construction": true});
            skLineSegment(sketch, "E27.3.10.0", {"start": v(35.03, -39.3) * mm, "end": v(39.3, -35.03) * mm});
            skCircle(sketch, "E27.6.10.0", {"center": v(30.27, -30.27) * mm, "radius": 2 * mm});
            skLineSegment(sketch, "E27.7.10.0", {"start": v(42.45, -35.03) * mm, "end": v(46.72, -39.3) * mm});
            skLineSegment(sketch, "E27.8.10.0", {"start": v(40.88, -40.88) * mm, "end": v(30.27, -30.27) * mm, "construction": true});
            skCircle(sketch, "E27.11.10.0", {"center": v(55.36, -37) * mm, "radius": 2 * mm});
            skCircle(sketch, "E27.13.10.0", {"center": v(37, -55.36) * mm, "radius": 2 * mm});
            skLineSegment(sketch, "E27.15.10.0", {"start": v(35.03, -42.45) * mm, "end": v(39.3, -46.72) * mm});
            skArc(sketch, "E27.18.10.0", {"start": v(42.45, -46.72) * mm, "mid": v(40.88, -45.33) * mm, "end": v(39.3, -46.72) * mm, "construction": true});
            skPoint(sketch, "E27.22.10.0", {"position": v(40.88, -40.88) * mm});
            skLineSegment(sketch, "E27.23.10.0", {"start": v(40.88, -40.88) * mm, "end": v(40.88, -48.3) * mm, "construction": true});
            skLineSegment(sketch, "E27.26.10.0", {"start": v(42.45, -46.72) * mm, "end": v(46.72, -42.45) * mm});
            skPoint(sketch, "E27.29.10.0", {"position": v(40.88, -40.88) * mm});
            skArc(sketch, "E27.30.10.0", {"start": v(42.45, -35.03) * mm, "mid": v(40.88, -33.25) * mm, "end": v(39.3, -35.03) * mm});
            skPoint(sketch, "E27.34.10.0", {"position": v(40.88, -40.88) * mm});
            skLineSegment(sketch, "E27.35.10.0", {"start": v(40.88, -33.45) * mm, "end": v(42.45, -35.03) * mm, "construction": true});
            skLineSegment(sketch, "E27.38.10.0", {"start": v(46.72, -42.45) * mm, "end": v(48.3, -40.88) * mm, "construction": true});
            skArc(sketch, "E27.41.10.0", {"start": v(46.72, -42.45) * mm, "mid": v(48.5, -40.88) * mm, "end": v(46.72, -39.3) * mm});
            skLineSegment(sketch, "E27.45.10.0", {"start": v(33.45, -40.88) * mm, "end": v(35.03, -42.45) * mm, "construction": true});
            skPoint(sketch, "E27.48.10.0", {"position": v(40.88, -40.88) * mm});
            skLineSegment(sketch, "E27.49.10.0", {"start": v(39.3, -35.03) * mm, "end": v(40.88, -33.45) * mm, "construction": true});
            skArc(sketch, "E27.52.10.0", {"start": v(35.03, -39.3) * mm, "mid": v(33.25, -40.88) * mm, "end": v(35.03, -42.45) * mm});
            skLineSegment(sketch, "E27.56.10.0", {"start": v(33.45, -40.88) * mm, "end": v(35.03, -39.3) * mm, "construction": true});
            skLineSegment(sketch, "E27.59.10.0", {"start": v(46.72, -39.3) * mm, "end": v(48.3, -40.88) * mm, "construction": true});
            skPoint(sketch, "E27.62.10.0", {"position": v(40.88, -40.88) * mm});
            skPoint(sketch, "E27.63.10.0", {"position": v(40.88, -40.88) * mm});
            skLineSegment(sketch, "E27.64.10.0", {"start": v(39.3, -46.72) * mm, "end": v(40.88, -48.3) * mm, "construction": true});
            skArc(sketch, "E27.67.10.0", {"start": v(39.3, -46.72) * mm, "mid": v(40.88, -48.5) * mm, "end": v(42.45, -46.72) * mm});
            skLineSegment(sketch, "E27.71.10.0", {"start": v(40.88, -48.3) * mm, "end": v(40.88, -48.5) * mm, "construction": true});
            skLineSegment(sketch, "E27.74.10.0", {"start": v(40.88, -48.3) * mm, "end": v(42.45, -46.72) * mm, "construction": true});
            skLineSegment(sketch, "E27.3.11.0", {"start": v(47.4, -22.9) * mm, "end": v(49.71, -17.32) * mm});
            skCircle(sketch, "E27.6.11.0", {"center": v(39.55, -16.38) * mm, "radius": 2 * mm});
            skLineSegment(sketch, "E27.7.11.0", {"start": v(52.62, -16.12) * mm, "end": v(58.2, -18.43) * mm});
            skLineSegment(sketch, "E27.8.11.0", {"start": v(53.4, -22.12) * mm, "end": v(39.55, -16.38) * mm, "construction": true});
            skCircle(sketch, "E27.11.11.0", {"center": v(65.3, -13) * mm, "radius": 2 * mm});
            skCircle(sketch, "E27.13.11.0", {"center": v(55.36, -37) * mm, "radius": 2 * mm});
            skLineSegment(sketch, "E27.15.11.0", {"start": v(48.6, -25.82) * mm, "end": v(54.19, -28.13) * mm});
            skArc(sketch, "E27.18.11.0", {"start": v(57.1, -26.92) * mm, "mid": v(55.1, -26.23) * mm, "end": v(54.19, -28.13) * mm, "construction": true});
            skPoint(sketch, "E27.22.11.0", {"position": v(53.4, -22.12) * mm});
            skLineSegment(sketch, "E27.23.11.0", {"start": v(53.4, -22.12) * mm, "end": v(56.25, -28.98) * mm, "construction": true});
            skLineSegment(sketch, "E27.26.11.0", {"start": v(57.1, -26.92) * mm, "end": v(59.41, -21.34) * mm});
            skPoint(sketch, "E27.29.11.0", {"position": v(53.4, -22.12) * mm});
            skArc(sketch, "E27.30.11.0", {"start": v(52.62, -16.12) * mm, "mid": v(50.49, -15.08) * mm, "end": v(49.71, -17.32) * mm});
            skPoint(sketch, "E27.34.11.0", {"position": v(53.4, -22.12) * mm});
            skLineSegment(sketch, "E27.35.11.0", {"start": v(50.57, -15.26) * mm, "end": v(52.62, -16.12) * mm, "construction": true});
            skLineSegment(sketch, "E27.38.11.0", {"start": v(59.41, -21.34) * mm, "end": v(60.27, -19.28) * mm, "construction": true});
            skArc(sketch, "E27.41.11.0", {"start": v(59.41, -21.34) * mm, "mid": v(60.45, -19.2) * mm, "end": v(58.2, -18.43) * mm});
            skLineSegment(sketch, "E27.45.11.0", {"start": v(46.55, -24.96) * mm, "end": v(48.6, -25.82) * mm, "construction": true});
            skPoint(sketch, "E27.48.11.0", {"position": v(53.4, -22.12) * mm});
            skLineSegment(sketch, "E27.49.11.0", {"start": v(49.71, -17.32) * mm, "end": v(50.57, -15.26) * mm, "construction": true});
            skArc(sketch, "E27.52.11.0", {"start": v(47.4, -22.9) * mm, "mid": v(46.36, -25.04) * mm, "end": v(48.6, -25.82) * mm});
            skLineSegment(sketch, "E27.56.11.0", {"start": v(46.55, -24.96) * mm, "end": v(47.4, -22.9) * mm, "construction": true});
            skLineSegment(sketch, "E27.59.11.0", {"start": v(58.2, -18.43) * mm, "end": v(60.27, -19.28) * mm, "construction": true});
            skPoint(sketch, "E27.62.11.0", {"position": v(53.4, -22.12) * mm});
            skPoint(sketch, "E27.63.11.0", {"position": v(53.4, -22.12) * mm});
            skLineSegment(sketch, "E27.64.11.0", {"start": v(54.19, -28.13) * mm, "end": v(56.25, -28.98) * mm, "construction": true});
            skArc(sketch, "E27.67.11.0", {"start": v(54.19, -28.13) * mm, "mid": v(56.32, -29.17) * mm, "end": v(57.1, -26.92) * mm});
            skLineSegment(sketch, "E27.71.11.0", {"start": v(56.25, -28.98) * mm, "end": v(56.32, -29.17) * mm, "construction": true});
            skLineSegment(sketch, "E27.74.11.0", {"start": v(56.25, -28.98) * mm, "end": v(57.1, -26.92) * mm, "construction": true});
            skLineSegment(sketch, "E27.3.12.0", {"start": v(52.56, -3.02) * mm, "end": v(52.56, 3.02) * mm});
            skCircle(sketch, "E27.6.12.0", {"center": v(42.8, 0) * mm, "radius": 2 * mm});
            skLineSegment(sketch, "E27.7.12.0", {"start": v(54.79, 5.25) * mm, "end": v(60.83, 5.25) * mm});
            skLineSegment(sketch, "E27.8.12.0", {"start": v(57.8, 0) * mm, "end": v(42.8, 0) * mm, "construction": true});
            skCircle(sketch, "E27.11.12.0", {"center": v(65.3, 13) * mm, "radius": 2 * mm});
            skCircle(sketch, "E27.13.12.0", {"center": v(65.3, -13) * mm, "radius": 2 * mm});
            skLineSegment(sketch, "E27.15.12.0", {"start": v(54.79, -5.25) * mm, "end": v(60.83, -5.25) * mm});
            skArc(sketch, "E27.18.12.0", {"start": v(63.06, -3.02) * mm, "mid": v(60.95, -3.15) * mm, "end": v(60.83, -5.25) * mm, "construction": true});
            skPoint(sketch, "E27.22.12.0", {"position": v(57.8, 0) * mm});
            skLineSegment(sketch, "E27.23.12.0", {"start": v(57.8, 0) * mm, "end": v(63.06, -5.25) * mm, "construction": true});
            skLineSegment(sketch, "E27.26.12.0", {"start": v(63.06, -3.02) * mm, "end": v(63.06, 3.02) * mm});
            skPoint(sketch, "E27.29.12.0", {"position": v(57.8, 0) * mm});
            skArc(sketch, "E27.30.12.0", {"start": v(54.79, 5.25) * mm, "mid": v(52.42, 5.4) * mm, "end": v(52.56, 3.02) * mm});
            skPoint(sketch, "E27.34.12.0", {"position": v(57.8, 0) * mm});
            skLineSegment(sketch, "E27.35.12.0", {"start": v(52.56, 5.25) * mm, "end": v(54.79, 5.25) * mm, "construction": true});
            skLineSegment(sketch, "E27.38.12.0", {"start": v(63.06, 3.02) * mm, "end": v(63.06, 5.25) * mm, "construction": true});
            skArc(sketch, "E27.41.12.0", {"start": v(63.06, 3.02) * mm, "mid": v(63.2, 5.4) * mm, "end": v(60.83, 5.25) * mm});
            skLineSegment(sketch, "E27.45.12.0", {"start": v(52.56, -5.25) * mm, "end": v(54.79, -5.25) * mm, "construction": true});
            skPoint(sketch, "E27.48.12.0", {"position": v(57.8, 0) * mm});
            skLineSegment(sketch, "E27.49.12.0", {"start": v(52.56, 3.02) * mm, "end": v(52.56, 5.25) * mm, "construction": true});
            skArc(sketch, "E27.52.12.0", {"start": v(52.56, -3.02) * mm, "mid": v(52.42, -5.4) * mm, "end": v(54.79, -5.25) * mm});
            skLineSegment(sketch, "E27.56.12.0", {"start": v(52.56, -5.25) * mm, "end": v(52.56, -3.02) * mm, "construction": true});
            skLineSegment(sketch, "E27.59.12.0", {"start": v(60.83, 5.25) * mm, "end": v(63.06, 5.25) * mm, "construction": true});
            skPoint(sketch, "E27.62.12.0", {"position": v(57.8, 0) * mm});
            skPoint(sketch, "E27.63.12.0", {"position": v(57.8, 0) * mm});
            skLineSegment(sketch, "E27.64.12.0", {"start": v(60.83, -5.25) * mm, "end": v(63.06, -5.25) * mm, "construction": true});
            skArc(sketch, "E27.67.12.0", {"start": v(60.83, -5.25) * mm, "mid": v(63.2, -5.4) * mm, "end": v(63.06, -3.02) * mm});
            skLineSegment(sketch, "E27.71.12.0", {"start": v(63.06, -5.25) * mm, "end": v(63.2, -5.4) * mm, "construction": true});
            skLineSegment(sketch, "E27.74.12.0", {"start": v(63.06, -5.25) * mm, "end": v(63.06, -3.02) * mm, "construction": true});
            skLineSegment(sketch, "E27.3.13.0", {"start": v(49.71, 17.32) * mm, "end": v(47.4, 22.9) * mm});
            skCircle(sketch, "E27.6.13.0", {"center": v(39.55, 16.38) * mm, "radius": 2 * mm});
            skLineSegment(sketch, "E27.7.13.0", {"start": v(48.6, 25.82) * mm, "end": v(54.19, 28.13) * mm});
            skLineSegment(sketch, "E27.8.13.0", {"start": v(53.4, 22.12) * mm, "end": v(39.55, 16.38) * mm, "construction": true});
            skCircle(sketch, "E27.11.13.0", {"center": v(55.36, 37) * mm, "radius": 2 * mm});
            skCircle(sketch, "E27.13.13.0", {"center": v(65.3, 13) * mm, "radius": 2 * mm});
            skLineSegment(sketch, "E27.15.13.0", {"start": v(52.62, 16.12) * mm, "end": v(58.2, 18.43) * mm});
            skArc(sketch, "E27.18.13.0", {"start": v(59.41, 21.34) * mm, "mid": v(57.52, 20.42) * mm, "end": v(58.2, 18.43) * mm, "construction": true});
            skPoint(sketch, "E27.22.13.0", {"position": v(53.4, 22.12) * mm});
            skLineSegment(sketch, "E27.23.13.0", {"start": v(53.4, 22.12) * mm, "end": v(60.27, 19.28) * mm, "construction": true});
            skLineSegment(sketch, "E27.26.13.0", {"start": v(59.41, 21.34) * mm, "end": v(57.1, 26.92) * mm});
            skPoint(sketch, "E27.29.13.0", {"position": v(53.4, 22.12) * mm});
            skArc(sketch, "E27.30.13.0", {"start": v(48.6, 25.82) * mm, "mid": v(46.36, 25.04) * mm, "end": v(47.4, 22.9) * mm});
            skPoint(sketch, "E27.34.13.0", {"position": v(53.4, 22.12) * mm});
            skLineSegment(sketch, "E27.35.13.0", {"start": v(46.55, 24.96) * mm, "end": v(48.6, 25.82) * mm, "construction": true});
            skLineSegment(sketch, "E27.38.13.0", {"start": v(57.1, 26.92) * mm, "end": v(56.25, 28.98) * mm, "construction": true});
            skArc(sketch, "E27.41.13.0", {"start": v(57.1, 26.92) * mm, "mid": v(56.32, 29.17) * mm, "end": v(54.19, 28.13) * mm});
            skLineSegment(sketch, "E27.45.13.0", {"start": v(50.57, 15.26) * mm, "end": v(52.62, 16.12) * mm, "construction": true});
            skPoint(sketch, "E27.48.13.0", {"position": v(53.4, 22.12) * mm});
            skLineSegment(sketch, "E27.49.13.0", {"start": v(47.4, 22.9) * mm, "end": v(46.55, 24.96) * mm, "construction": true});
            skArc(sketch, "E27.52.13.0", {"start": v(49.71, 17.32) * mm, "mid": v(50.49, 15.08) * mm, "end": v(52.62, 16.12) * mm});
            skLineSegment(sketch, "E27.56.13.0", {"start": v(50.57, 15.26) * mm, "end": v(49.71, 17.32) * mm, "construction": true});
            skLineSegment(sketch, "E27.59.13.0", {"start": v(54.19, 28.13) * mm, "end": v(56.25, 28.98) * mm, "construction": true});
            skPoint(sketch, "E27.62.13.0", {"position": v(53.4, 22.12) * mm});
            skPoint(sketch, "E27.63.13.0", {"position": v(53.4, 22.12) * mm});
            skLineSegment(sketch, "E27.64.13.0", {"start": v(58.2, 18.43) * mm, "end": v(60.27, 19.28) * mm, "construction": true});
            skArc(sketch, "E27.67.13.0", {"start": v(58.2, 18.43) * mm, "mid": v(60.45, 19.2) * mm, "end": v(59.41, 21.34) * mm});
            skLineSegment(sketch, "E27.71.13.0", {"start": v(60.27, 19.28) * mm, "end": v(60.45, 19.2) * mm, "construction": true});
            skLineSegment(sketch, "E27.74.13.0", {"start": v(60.27, 19.28) * mm, "end": v(59.41, 21.34) * mm, "construction": true});
            skLineSegment(sketch, "E27.3.14.0", {"start": v(39.3, 35.03) * mm, "end": v(35.03, 39.3) * mm});
            skCircle(sketch, "E27.6.14.0", {"center": v(30.27, 30.27) * mm, "radius": 2 * mm});
            skLineSegment(sketch, "E27.7.14.0", {"start": v(35.03, 42.45) * mm, "end": v(39.3, 46.72) * mm});
            skLineSegment(sketch, "E27.8.14.0", {"start": v(40.88, 40.88) * mm, "end": v(30.27, 30.27) * mm, "construction": true});
            skCircle(sketch, "E27.11.14.0", {"center": v(37, 55.36) * mm, "radius": 2 * mm});
            skCircle(sketch, "E27.13.14.0", {"center": v(55.36, 37) * mm, "radius": 2 * mm});
            skLineSegment(sketch, "E27.15.14.0", {"start": v(42.45, 35.03) * mm, "end": v(46.72, 39.3) * mm});
            skArc(sketch, "E27.18.14.0", {"start": v(46.72, 42.45) * mm, "mid": v(45.33, 40.88) * mm, "end": v(46.72, 39.3) * mm, "construction": true});
            skPoint(sketch, "E27.22.14.0", {"position": v(40.88, 40.88) * mm});
            skLineSegment(sketch, "E27.23.14.0", {"start": v(40.88, 40.88) * mm, "end": v(48.3, 40.88) * mm, "construction": true});
            skLineSegment(sketch, "E27.26.14.0", {"start": v(46.72, 42.45) * mm, "end": v(42.45, 46.72) * mm});
            skPoint(sketch, "E27.29.14.0", {"position": v(40.88, 40.88) * mm});
            skArc(sketch, "E27.30.14.0", {"start": v(35.03, 42.45) * mm, "mid": v(33.25, 40.88) * mm, "end": v(35.03, 39.3) * mm});
            skPoint(sketch, "E27.34.14.0", {"position": v(40.88, 40.88) * mm});
            skLineSegment(sketch, "E27.35.14.0", {"start": v(33.45, 40.88) * mm, "end": v(35.03, 42.45) * mm, "construction": true});
            skLineSegment(sketch, "E27.38.14.0", {"start": v(42.45, 46.72) * mm, "end": v(40.88, 48.3) * mm, "construction": true});
            skArc(sketch, "E27.41.14.0", {"start": v(42.45, 46.72) * mm, "mid": v(40.88, 48.5) * mm, "end": v(39.3, 46.72) * mm});
            skLineSegment(sketch, "E27.45.14.0", {"start": v(40.88, 33.45) * mm, "end": v(42.45, 35.03) * mm, "construction": true});
            skPoint(sketch, "E27.48.14.0", {"position": v(40.88, 40.88) * mm});
            skLineSegment(sketch, "E27.49.14.0", {"start": v(35.03, 39.3) * mm, "end": v(33.45, 40.88) * mm, "construction": true});
            skArc(sketch, "E27.52.14.0", {"start": v(39.3, 35.03) * mm, "mid": v(40.88, 33.25) * mm, "end": v(42.45, 35.03) * mm});
            skLineSegment(sketch, "E27.56.14.0", {"start": v(40.88, 33.45) * mm, "end": v(39.3, 35.03) * mm, "construction": true});
            skLineSegment(sketch, "E27.59.14.0", {"start": v(39.3, 46.72) * mm, "end": v(40.88, 48.3) * mm, "construction": true});
            skPoint(sketch, "E27.62.14.0", {"position": v(40.88, 40.88) * mm});
            skPoint(sketch, "E27.63.14.0", {"position": v(40.88, 40.88) * mm});
            skLineSegment(sketch, "E27.64.14.0", {"start": v(46.72, 39.3) * mm, "end": v(48.3, 40.88) * mm, "construction": true});
            skArc(sketch, "E27.67.14.0", {"start": v(46.72, 39.3) * mm, "mid": v(48.5, 40.88) * mm, "end": v(46.72, 42.45) * mm});
            skLineSegment(sketch, "E27.71.14.0", {"start": v(48.3, 40.88) * mm, "end": v(48.5, 40.88) * mm, "construction": true});
            skLineSegment(sketch, "E27.74.14.0", {"start": v(48.3, 40.88) * mm, "end": v(46.72, 42.45) * mm, "construction": true});
            skLineSegment(sketch, "E27.3.15.0", {"start": v(22.9, 47.4) * mm, "end": v(17.32, 49.71) * mm});
            skCircle(sketch, "E27.6.15.0", {"center": v(16.38, 39.55) * mm, "radius": 2 * mm});
            skLineSegment(sketch, "E27.7.15.0", {"start": v(16.12, 52.62) * mm, "end": v(18.43, 58.2) * mm});
            skLineSegment(sketch, "E27.8.15.0", {"start": v(22.12, 53.4) * mm, "end": v(16.38, 39.55) * mm, "construction": true});
            skCircle(sketch, "E27.13.15.0", {"center": v(37, 55.36) * mm, "radius": 2 * mm});
            skLineSegment(sketch, "E27.15.15.0", {"start": v(25.82, 48.6) * mm, "end": v(28.13, 54.19) * mm});
            skArc(sketch, "E27.18.15.0", {"start": v(26.92, 57.1) * mm, "mid": v(26.23, 55.1) * mm, "end": v(28.13, 54.19) * mm, "construction": true});
            skPoint(sketch, "E27.22.15.0", {"position": v(22.12, 53.4) * mm});
            skLineSegment(sketch, "E27.23.15.0", {"start": v(22.12, 53.4) * mm, "end": v(28.98, 56.25) * mm, "construction": true});
            skLineSegment(sketch, "E27.26.15.0", {"start": v(26.92, 57.1) * mm, "end": v(21.34, 59.41) * mm});
            skPoint(sketch, "E27.29.15.0", {"position": v(22.12, 53.4) * mm});
            skArc(sketch, "E27.30.15.0", {"start": v(16.12, 52.62) * mm, "mid": v(15.08, 50.49) * mm, "end": v(17.32, 49.71) * mm});
            skPoint(sketch, "E27.34.15.0", {"position": v(22.12, 53.4) * mm});
            skLineSegment(sketch, "E27.35.15.0", {"start": v(15.26, 50.57) * mm, "end": v(16.12, 52.62) * mm, "construction": true});
            skLineSegment(sketch, "E27.38.15.0", {"start": v(21.34, 59.41) * mm, "end": v(19.28, 60.27) * mm, "construction": true});
            skArc(sketch, "E27.41.15.0", {"start": v(21.34, 59.41) * mm, "mid": v(19.2, 60.45) * mm, "end": v(18.43, 58.2) * mm});
            skLineSegment(sketch, "E27.45.15.0", {"start": v(24.96, 46.55) * mm, "end": v(25.82, 48.6) * mm, "construction": true});
            skPoint(sketch, "E27.48.15.0", {"position": v(22.12, 53.4) * mm});
            skLineSegment(sketch, "E27.49.15.0", {"start": v(17.32, 49.71) * mm, "end": v(15.26, 50.57) * mm, "construction": true});
            skArc(sketch, "E27.52.15.0", {"start": v(22.9, 47.4) * mm, "mid": v(25.04, 46.36) * mm, "end": v(25.82, 48.6) * mm});
            skLineSegment(sketch, "E27.56.15.0", {"start": v(24.96, 46.55) * mm, "end": v(22.9, 47.4) * mm, "construction": true});
            skLineSegment(sketch, "E27.59.15.0", {"start": v(18.43, 58.2) * mm, "end": v(19.28, 60.27) * mm, "construction": true});
            skPoint(sketch, "E27.62.15.0", {"position": v(22.12, 53.4) * mm});
            skPoint(sketch, "E27.63.15.0", {"position": v(22.12, 53.4) * mm});
            skLineSegment(sketch, "E27.64.15.0", {"start": v(28.13, 54.19) * mm, "end": v(28.98, 56.25) * mm, "construction": true});
            skArc(sketch, "E27.67.15.0", {"start": v(28.13, 54.19) * mm, "mid": v(29.17, 56.32) * mm, "end": v(26.92, 57.1) * mm});
            skLineSegment(sketch, "E27.71.15.0", {"start": v(28.98, 56.25) * mm, "end": v(29.17, 56.32) * mm, "construction": true});
            skLineSegment(sketch, "E27.74.15.0", {"start": v(28.98, 56.25) * mm, "end": v(26.92, 57.1) * mm, "construction": true});
            skLineSegment(sketch, "E28.bottom", {"start": v(-2, 63.06) * mm, "end": v(2, 63.06) * mm});
            skLineSegment(sketch, "E28.top", {"start": v(-2, 73.06) * mm, "end": v(2, 73.06) * mm});
            skLineSegment(sketch, "E28.left", {"start": v(-2, 63.06) * mm, "end": v(-2, 73.06) * mm});
            skLineSegment(sketch, "E28.right", {"start": v(2, 63.06) * mm, "end": v(2, 73.06) * mm});
            skPoint(sketch, "E29", {"position": v(0, 73.06) * mm});
            skPoint(sketch, "E30", {"position": v(0, 63.06) * mm});
            skLineSegment(sketch, "E31.1.0", {"start": v(-25.98, 57.5) * mm, "end": v(-29.8, 66.73) * mm});
            skLineSegment(sketch, "E31.1.1", {"start": v(-29.8, 66.73) * mm, "end": v(-26.1, 68.26) * mm});
            skLineSegment(sketch, "E31.1.2", {"start": v(-22.28, 59.02) * mm, "end": v(-26.1, 68.26) * mm});
            skLineSegment(sketch, "E31.2.0", {"start": v(-46, 43.17) * mm, "end": v(-53.07, 50.24) * mm});
            skLineSegment(sketch, "E31.2.1", {"start": v(-53.07, 50.24) * mm, "end": v(-50.24, 53.07) * mm});
            skLineSegment(sketch, "E31.2.2", {"start": v(-43.17, 46) * mm, "end": v(-50.24, 53.07) * mm});
            skLineSegment(sketch, "E31.3.0", {"start": v(-59.02, 22.28) * mm, "end": v(-68.26, 26.1) * mm});
            skLineSegment(sketch, "E31.3.1", {"start": v(-68.26, 26.1) * mm, "end": v(-66.73, 29.8) * mm});
            skLineSegment(sketch, "E31.3.2", {"start": v(-57.5, 25.98) * mm, "end": v(-66.73, 29.8) * mm});
            skLineSegment(sketch, "E31.4.0", {"start": v(-63.06, -2) * mm, "end": v(-73.06, -2) * mm});
            skLineSegment(sketch, "E31.4.1", {"start": v(-73.06, -2) * mm, "end": v(-73.06, 2) * mm});
            skLineSegment(sketch, "E31.4.2", {"start": v(-63.06, 2) * mm, "end": v(-73.06, 2) * mm});
            skLineSegment(sketch, "E31.5.0", {"start": v(-57.5, -25.98) * mm, "end": v(-66.73, -29.8) * mm});
            skLineSegment(sketch, "E31.5.1", {"start": v(-66.73, -29.8) * mm, "end": v(-68.26, -26.1) * mm});
            skLineSegment(sketch, "E31.5.2", {"start": v(-59.02, -22.28) * mm, "end": v(-68.26, -26.1) * mm});
            skLineSegment(sketch, "E31.6.0", {"start": v(-43.17, -46) * mm, "end": v(-50.24, -53.07) * mm});
            skLineSegment(sketch, "E31.6.1", {"start": v(-50.24, -53.07) * mm, "end": v(-53.07, -50.24) * mm});
            skLineSegment(sketch, "E31.6.2", {"start": v(-46, -43.17) * mm, "end": v(-53.07, -50.24) * mm});
            skLineSegment(sketch, "E31.7.0", {"start": v(-22.28, -59.02) * mm, "end": v(-26.1, -68.26) * mm});
            skLineSegment(sketch, "E31.7.1", {"start": v(-26.1, -68.26) * mm, "end": v(-29.8, -66.73) * mm});
            skLineSegment(sketch, "E31.7.2", {"start": v(-25.98, -57.5) * mm, "end": v(-29.8, -66.73) * mm});
            skLineSegment(sketch, "E31.8.0", {"start": v(2, -63.06) * mm, "end": v(2, -73.06) * mm});
            skLineSegment(sketch, "E31.8.1", {"start": v(2, -73.06) * mm, "end": v(-2, -73.06) * mm});
            skLineSegment(sketch, "E31.8.2", {"start": v(-2, -63.06) * mm, "end": v(-2, -73.06) * mm});
            skLineSegment(sketch, "E31.9.0", {"start": v(25.98, -57.5) * mm, "end": v(29.8, -66.73) * mm});
            skLineSegment(sketch, "E31.9.1", {"start": v(29.8, -66.73) * mm, "end": v(26.1, -68.26) * mm});
            skLineSegment(sketch, "E31.9.2", {"start": v(22.28, -59.02) * mm, "end": v(26.1, -68.26) * mm});
            skLineSegment(sketch, "E31.10.0", {"start": v(46, -43.17) * mm, "end": v(53.07, -50.24) * mm});
            skLineSegment(sketch, "E31.10.1", {"start": v(53.07, -50.24) * mm, "end": v(50.24, -53.07) * mm});
            skLineSegment(sketch, "E31.10.2", {"start": v(43.17, -46) * mm, "end": v(50.24, -53.07) * mm});
            skLineSegment(sketch, "E31.11.0", {"start": v(59.02, -22.28) * mm, "end": v(68.26, -26.1) * mm});
            skLineSegment(sketch, "E31.11.1", {"start": v(68.26, -26.1) * mm, "end": v(66.73, -29.8) * mm});
            skLineSegment(sketch, "E31.11.2", {"start": v(57.5, -25.98) * mm, "end": v(66.73, -29.8) * mm});
            skLineSegment(sketch, "E31.12.0", {"start": v(63.06, 2) * mm, "end": v(73.06, 2) * mm});
            skLineSegment(sketch, "E31.12.1", {"start": v(73.06, 2) * mm, "end": v(73.06, -2) * mm});
            skLineSegment(sketch, "E31.12.2", {"start": v(63.06, -2) * mm, "end": v(73.06, -2) * mm});
            skLineSegment(sketch, "E31.13.0", {"start": v(57.5, 25.98) * mm, "end": v(66.73, 29.8) * mm});
            skLineSegment(sketch, "E31.13.1", {"start": v(66.73, 29.8) * mm, "end": v(68.26, 26.1) * mm});
            skLineSegment(sketch, "E31.13.2", {"start": v(59.02, 22.28) * mm, "end": v(68.26, 26.1) * mm});
            skLineSegment(sketch, "E31.14.0", {"start": v(43.17, 46) * mm, "end": v(50.24, 53.07) * mm});
            skLineSegment(sketch, "E31.14.1", {"start": v(50.24, 53.07) * mm, "end": v(53.07, 50.24) * mm});
            skLineSegment(sketch, "E31.14.2", {"start": v(46, 43.17) * mm, "end": v(53.07, 50.24) * mm});
            skLineSegment(sketch, "E31.15.0", {"start": v(22.28, 59.02) * mm, "end": v(26.1, 68.26) * mm});
            skLineSegment(sketch, "E31.15.1", {"start": v(26.1, 68.26) * mm, "end": v(29.8, 66.73) * mm});
            skLineSegment(sketch, "E31.15.2", {"start": v(25.98, 57.5) * mm, "end": v(29.8, 66.73) * mm});
            skLineSegment(sketch, "E32.bottom", {"start": v(5.25, 19.75) * mm, "end": v(3.02, 19.75) * mm, "construction": true});
            skLineSegment(sketch, "E32.top", {"start": v(5.25, 30.25) * mm, "end": v(3.02, 30.25) * mm, "construction": true});
            skLineSegment(sketch, "E32.left", {"start": v(5.25, 19.75) * mm, "end": v(5.25, 19.75) * mm});
            skLineSegment(sketch, "E32.right", {"start": v(-5.25, 19.75) * mm, "end": v(-5.25, 21.98) * mm, "construction": true});
            skPoint(sketch, "E32.middle", {"position": v(0, 25) * mm});
            skLineSegment(sketch, "E33", {"start": v(0, 25) * mm, "end": v(5.25, 30.25) * mm, "construction": true});
            skLineSegment(sketch, "E34", {"start": v(5.25, 30.25) * mm, "end": v(5.4, 30.4) * mm, "construction": true});
            skArc(sketch, "E35", {"start": v(5.25, 28.02) * mm, "mid": v(5.4, 30.4) * mm, "end": v(3.02, 30.25) * mm});
            skArc(sketch, "E36", {"start": v(3.02, 30.25) * mm, "mid": v(3.15, 28.15) * mm, "end": v(5.25, 28.02) * mm, "construction": true});
            skLineSegment(sketch, "E37", {"start": v(5.25, 28.02) * mm, "end": v(5.25, 30.25) * mm, "construction": true});
            skLineSegment(sketch, "E38", {"start": v(5.25, 19.75) * mm, "end": v(5.25, 21.98) * mm, "construction": true});
            skLineSegment(sketch, "E39", {"start": v(3.02, 30.25) * mm, "end": v(3.02, 30.25) * mm});
            skLineSegment(sketch, "E40", {"start": v(-5.25, 30.25) * mm, "end": v(-5.25, 30.25) * mm});
            skArc(sketch, "E41.1.0", {"start": v(-3.02, 30.25) * mm, "mid": v(-5.4, 30.4) * mm, "end": v(-5.25, 28.02) * mm});
            skArc(sketch, "E41.2.0", {"start": v(-5.25, 21.98) * mm, "mid": v(-5.4, 19.6) * mm, "end": v(-3.02, 19.75) * mm});
            skArc(sketch, "E42.2.3.0", {"start": v(3.02, 19.75) * mm, "mid": v(5.4, 19.6) * mm, "end": v(5.25, 21.98) * mm});
            skLineSegment(sketch, "E43", {"start": v(-5.25, 28.02) * mm, "end": v(-5.25, 30.25) * mm, "construction": true});
            skLineSegment(sketch, "E44", {"start": v(-5.25, 21.98) * mm, "end": v(-5.25, 28.02) * mm});
            skLineSegment(sketch, "E45", {"start": v(-3.02, 19.75) * mm, "end": v(-5.25, 19.75) * mm, "construction": true});
            skLineSegment(sketch, "E46", {"start": v(3.02, 19.75) * mm, "end": v(-3.02, 19.75) * mm});
            skLineSegment(sketch, "E47", {"start": v(3.02, 30.25) * mm, "end": v(-3.02, 30.25) * mm});
            skLineSegment(sketch, "E48", {"start": v(-3.02, 30.25) * mm, "end": v(-5.25, 30.25) * mm, "construction": true});
            skLineSegment(sketch, "E49", {"start": v(5.25, 21.98) * mm, "end": v(5.25, 28.02) * mm});
            skLineSegment(sketch, "E50", {"start": v(5.25, 28.02) * mm, "end": v(5.25, 28.02) * mm});
            skLineSegment(sketch, "E51.bottom", {"start": v(-2, 30.25) * mm, "end": v(2, 30.25) * mm});
            skPoint(sketch, "E52", {"position": v(0, 30.25) * mm});
            skLineSegment(sketch, "E53", {"start": v(0, 42.8) * mm, "end": v(0, 0) * mm, "construction": true});
            skLineSegment(sketch, "E54.1.0", {"start": v(-21.98, -5.25) * mm, "end": v(-28.02, -5.25) * mm});
            skLineSegment(sketch, "E54.1.1", {"start": v(-19.75, -5.25) * mm, "end": v(-21.98, -5.25) * mm, "construction": true});
            skPoint(sketch, "E54.1.2", {"position": v(-30.25, 0) * mm});
            skArc(sketch, "E54.1.3", {"start": v(-30.25, -3.02) * mm, "mid": v(-30.4, -5.4) * mm, "end": v(-28.02, -5.25) * mm});
            skArc(sketch, "E54.1.4", {"start": v(-21.98, -5.25) * mm, "mid": v(-19.6, -5.4) * mm, "end": v(-19.75, -3.02) * mm});
            skLineSegment(sketch, "E54.1.5", {"start": v(-28.02, -5.25) * mm, "end": v(-30.25, -5.25) * mm, "construction": true});
            skLineSegment(sketch, "E54.1.6", {"start": v(-19.75, -3.02) * mm, "end": v(-19.75, -5.25) * mm, "construction": true});
            skLineSegment(sketch, "E54.1.7", {"start": v(-19.75, 3.02) * mm, "end": v(-19.75, -3.02) * mm});
            skLineSegment(sketch, "E54.1.8", {"start": v(-30.25, -3.02) * mm, "end": v(-30.25, -5.25) * mm, "construction": true});
            skLineSegment(sketch, "E54.1.9", {"start": v(-21.98, 5.25) * mm, "end": v(-28.02, 5.25) * mm});
            skArc(sketch, "E54.1.11", {"start": v(-28.02, 5.25) * mm, "mid": v(-30.4, 5.4) * mm, "end": v(-30.25, 3.02) * mm});
            skPoint(sketch, "E54.1.12", {"position": v(-25, 0) * mm});
            skArc(sketch, "E54.1.13", {"start": v(-30.25, 3.02) * mm, "mid": v(-28.15, 3.15) * mm, "end": v(-28.02, 5.25) * mm, "construction": true});
            skLineSegment(sketch, "E54.1.14", {"start": v(-28.02, 5.25) * mm, "end": v(-30.25, 5.25) * mm, "construction": true});
            skArc(sketch, "E54.1.15", {"start": v(-19.75, 3.02) * mm, "mid": v(-19.6, 5.4) * mm, "end": v(-21.98, 5.25) * mm});
            skLineSegment(sketch, "E54.1.16", {"start": v(-19.75, 5.25) * mm, "end": v(-19.75, 3.02) * mm, "construction": true});
            skLineSegment(sketch, "E54.1.17", {"start": v(-30.25, 3.02) * mm, "end": v(-30.25, -3.02) * mm});
            skLineSegment(sketch, "E54.1.18", {"start": v(-30.25, 5.25) * mm, "end": v(-30.25, 3.02) * mm, "construction": true});
            skLineSegment(sketch, "E54.1.19", {"start": v(-30.25, -2) * mm, "end": v(-30.25, 2) * mm});
            skPoint(sketch, "E54.1.20", {"position": v(-25, 0) * mm});
            skLineSegment(sketch, "E54.1.21", {"start": v(-19.75, 5.25) * mm, "end": v(-21.98, 5.25) * mm, "construction": true});
            skPoint(sketch, "E54.1.22", {"position": v(-25, 0) * mm});
            skPoint(sketch, "E54.1.23", {"position": v(-25, 0) * mm});
            skPoint(sketch, "E54.1.24", {"position": v(-25, 0) * mm});
            skLineSegment(sketch, "E54.1.25", {"start": v(-30.25, 5.25) * mm, "end": v(-30.4, 5.4) * mm, "construction": true});
            skPoint(sketch, "E54.1.26", {"position": v(-25, 0) * mm});
            skLineSegment(sketch, "E54.2.0", {"start": v(5.25, -21.98) * mm, "end": v(5.25, -28.02) * mm});
            skLineSegment(sketch, "E54.2.1", {"start": v(5.25, -19.75) * mm, "end": v(5.25, -21.98) * mm, "construction": true});
            skPoint(sketch, "E54.2.2", {"position": v(0, -30.25) * mm});
            skArc(sketch, "E54.2.3", {"start": v(3.02, -30.25) * mm, "mid": v(5.4, -30.4) * mm, "end": v(5.25, -28.02) * mm});
            skArc(sketch, "E54.2.4", {"start": v(5.25, -21.98) * mm, "mid": v(5.4, -19.6) * mm, "end": v(3.02, -19.75) * mm});
            skLineSegment(sketch, "E54.2.5", {"start": v(5.25, -28.02) * mm, "end": v(5.25, -30.25) * mm, "construction": true});
            skLineSegment(sketch, "E54.2.6", {"start": v(3.02, -19.75) * mm, "end": v(5.25, -19.75) * mm, "construction": true});
            skLineSegment(sketch, "E54.2.7", {"start": v(-3.02, -19.75) * mm, "end": v(3.02, -19.75) * mm});
            skLineSegment(sketch, "E54.2.8", {"start": v(3.02, -30.25) * mm, "end": v(5.25, -30.25) * mm, "construction": true});
            skLineSegment(sketch, "E54.2.9", {"start": v(-5.25, -21.98) * mm, "end": v(-5.25, -28.02) * mm});
            skLineSegment(sketch, "E54.2.10", {"start": v(0, -25) * mm, "end": v(-5.25, -30.25) * mm, "construction": true});
            skArc(sketch, "E54.2.11", {"start": v(-5.25, -28.02) * mm, "mid": v(-5.4, -30.4) * mm, "end": v(-3.02, -30.25) * mm});
            skPoint(sketch, "E54.2.12", {"position": v(0, -25) * mm});
            skArc(sketch, "E54.2.13", {"start": v(-3.02, -30.25) * mm, "mid": v(-3.15, -28.15) * mm, "end": v(-5.25, -28.02) * mm, "construction": true});
            skLineSegment(sketch, "E54.2.14", {"start": v(-5.25, -28.02) * mm, "end": v(-5.25, -30.25) * mm, "construction": true});
            skArc(sketch, "E54.2.15", {"start": v(-3.02, -19.75) * mm, "mid": v(-5.4, -19.6) * mm, "end": v(-5.25, -21.98) * mm});
            skLineSegment(sketch, "E54.2.16", {"start": v(-5.25, -19.75) * mm, "end": v(-3.02, -19.75) * mm, "construction": true});
            skLineSegment(sketch, "E54.2.17", {"start": v(-3.02, -30.25) * mm, "end": v(3.02, -30.25) * mm});
            skLineSegment(sketch, "E54.2.18", {"start": v(-5.25, -30.25) * mm, "end": v(-3.02, -30.25) * mm, "construction": true});
            skLineSegment(sketch, "E54.2.19", {"start": v(2, -30.25) * mm, "end": v(-2, -30.25) * mm});
            skPoint(sketch, "E54.2.20", {"position": v(0, -25) * mm});
            skLineSegment(sketch, "E54.2.21", {"start": v(-5.25, -19.75) * mm, "end": v(-5.25, -21.98) * mm, "construction": true});
            skPoint(sketch, "E54.2.22", {"position": v(0, -25) * mm});
            skPoint(sketch, "E54.2.23", {"position": v(0, -25) * mm});
            skPoint(sketch, "E54.2.24", {"position": v(0, -25) * mm});
            skLineSegment(sketch, "E54.2.25", {"start": v(-5.25, -30.25) * mm, "end": v(-5.4, -30.4) * mm, "construction": true});
            skPoint(sketch, "E54.2.26", {"position": v(0, -25) * mm});
            skLineSegment(sketch, "E55.3.3.0", {"start": v(19.75, 5.25) * mm, "end": v(21.98, 5.25) * mm, "construction": true});
            skLineSegment(sketch, "E55.4.3.0", {"start": v(21.98, 5.25) * mm, "end": v(28.02, 5.25) * mm});
            skPoint(sketch, "E55.6.3.0", {"position": v(30.25, 0) * mm});
            skArc(sketch, "E55.7.3.0", {"start": v(30.25, 3.02) * mm, "mid": v(30.4, 5.4) * mm, "end": v(28.02, 5.25) * mm});
            skArc(sketch, "E55.11.3.0", {"start": v(21.98, 5.25) * mm, "mid": v(19.6, 5.4) * mm, "end": v(19.75, 3.02) * mm});
            skLineSegment(sketch, "E55.15.3.0", {"start": v(28.02, 5.25) * mm, "end": v(30.25, 5.25) * mm, "construction": true});
            skLineSegment(sketch, "E55.18.3.0", {"start": v(19.75, 3.02) * mm, "end": v(19.75, 5.25) * mm, "construction": true});
            skLineSegment(sketch, "E55.21.3.0", {"start": v(19.75, -3.02) * mm, "end": v(19.75, 3.02) * mm});
            skLineSegment(sketch, "E55.24.3.0", {"start": v(30.25, 3.02) * mm, "end": v(30.25, 5.25) * mm, "construction": true});
            skLineSegment(sketch, "E55.27.3.0", {"start": v(21.98, -5.25) * mm, "end": v(28.02, -5.25) * mm});
            skLineSegment(sketch, "E55.30.3.0", {"start": v(25, 0) * mm, "end": v(30.25, -5.25) * mm, "construction": true});
            skArc(sketch, "E55.33.3.0", {"start": v(28.02, -5.25) * mm, "mid": v(30.4, -5.4) * mm, "end": v(30.25, -3.02) * mm});
            skPoint(sketch, "E55.37.3.0", {"position": v(25, 0) * mm});
            skArc(sketch, "E55.38.3.0", {"start": v(30.25, -3.02) * mm, "mid": v(28.15, -3.15) * mm, "end": v(28.02, -5.25) * mm, "construction": true});
            skLineSegment(sketch, "E55.42.3.0", {"start": v(28.02, -5.25) * mm, "end": v(30.25, -5.25) * mm, "construction": true});
            skArc(sketch, "E55.45.3.0", {"start": v(19.75, -3.02) * mm, "mid": v(19.6, -5.4) * mm, "end": v(21.98, -5.25) * mm});
            skLineSegment(sketch, "E55.49.3.0", {"start": v(19.75, -5.25) * mm, "end": v(19.75, -3.02) * mm, "construction": true});
            skLineSegment(sketch, "E55.52.3.0", {"start": v(30.25, -3.02) * mm, "end": v(30.25, 3.02) * mm});
            skLineSegment(sketch, "E55.55.3.0", {"start": v(30.25, -5.25) * mm, "end": v(30.25, -3.02) * mm, "construction": true});
            skLineSegment(sketch, "E55.58.3.0", {"start": v(30.25, 2) * mm, "end": v(30.25, -2) * mm});
            skPoint(sketch, "E55.61.3.0", {"position": v(25, 0) * mm});
            skLineSegment(sketch, "E55.62.3.0", {"start": v(19.75, -5.25) * mm, "end": v(21.98, -5.25) * mm, "construction": true});
            skPoint(sketch, "E55.65.3.0", {"position": v(25, 0) * mm});
            skPoint(sketch, "E55.66.3.0", {"position": v(25, 0) * mm});
            skPoint(sketch, "E55.67.3.0", {"position": v(25, 0) * mm});
            skLineSegment(sketch, "E55.68.3.0", {"start": v(30.25, -5.25) * mm, "end": v(30.4, -5.4) * mm, "construction": true});
            skPoint(sketch, "E55.71.3.0", {"position": v(25, 0) * mm});
            skSolve(sketch);
        }
        {
            var Q0;
            Q0=qSketchRegion(id+"F0",true);
            extrude(context, id + "F1", {"entities" : qUnion([Q0]), "depth" : 1 * mm});
        }
        {
            var Q0;
            Q0=makeQuery(id+"F1.opExtrude","CAP_FACE",FACE,{"disambiguationData":[OSD([sQuery(id+"F0.wireOp",EDGE,"E0"),sQuery(id+"F0.wireOp",EDGE,"hH4bWqKN-iWDR-fp0z-Jon2-1weh1UKTDFdZ.bottom"),sQuery(id+"F0.wireOp",EDGE,"hH4bWqKN-iWDR-fp0z-Jon2-1weh1UKTDFdZ.top"),sQuery(id+"F0.wireOp",EDGE,"hH4bWqKN-iWDR-fp0z-Jon2-1weh1UKTDFdZ.left"),sQuery(id+"F0.wireOp",EDGE,"hH4bWqKN-iWDR-fp0z-Jon2-1weh1UKTDFdZ.right"),sQuery(id+"F0.wireOp",EDGE,"E7zOeCWY-U8Ve-haNj-cVaJ-LoHAemIPS7JA"),sQuery(id+"F0.wireOp",EDGE,"599eb16f-ceb1-4bc4-949a-59c5207a0cf7.2.0"),sQuery(id+"F0.wireOp",EDGE,"WxvxhokO-4ER6-JAze-Ogaa-00zI1Wum0iAN"),sQuery(id+"F0.wireOp",EDGE,"aaX6ALns-FgWH-aA4e-3TGY-vawF98CylBah"),sQuery(id+"F0.wireOp",EDGE,"KXN2FGoz-stmo-znhR-Zbhz-c4lYAjo9kMZA"),sQuery(id+"F0.wireOp",EDGE,"7iuNFIzY-911t-Fhu3-9f9n-fvbma6LIRfwR"),sQuery(id+"F0.wireOp",EDGE,"4bab01e7-d052-4abf-b01b-eb726d723c40.1.0"),sQuery(id+"F0.wireOp",EDGE,"4bab01e7-d052-4abf-b01b-eb726d723c40.1.1"),sQuery(id+"F0.wireOp",EDGE,"4bab01e7-d052-4abf-b01b-eb726d723c40.1.3"),sQuery(id+"F0.wireOp",EDGE,"4bab01e7-d052-4abf-b01b-eb726d723c40.1.4"),sQuery(id+"F0.wireOp",EDGE,"4bab01e7-d052-4abf-b01b-eb726d723c40.1.7"),sQuery(id+"F0.wireOp",EDGE,"4bab01e7-d052-4abf-b01b-eb726d723c40.1.8"),sQuery(id+"F0.wireOp",EDGE,"4bab01e7-d052-4abf-b01b-eb726d723c40.1.10"),sQuery(id+"F0.wireOp",EDGE,"4bab01e7-d052-4abf-b01b-eb726d723c40.1.11"),sQuery(id+"F0.wireOp",EDGE,"4bab01e7-d052-4abf-b01b-eb726d723c40.1.12"),sQuery(id+"F0.wireOp",EDGE,"4bab01e7-d052-4abf-b01b-eb726d723c40.1.13"),sQuery(id+"F0.wireOp",EDGE,"4bab01e7-d052-4abf-b01b-eb726d723c40.2.0"),sQuery(id+"F0.wireOp",EDGE,"4bab01e7-d052-4abf-b01b-eb726d723c40.2.1"),sQuery(id+"F0.wireOp",EDGE,"4bab01e7-d052-4abf-b01b-eb726d723c40.2.3"),sQuery(id+"F0.wireOp",EDGE,"4bab01e7-d052-4abf-b01b-eb726d723c40.2.4"),sQuery(id+"F0.wireOp",EDGE,"4bab01e7-d052-4abf-b01b-eb726d723c40.2.7"),sQuery(id+"F0.wireOp",EDGE,"4bab01e7-d052-4abf-b01b-eb726d723c40.2.8"),sQuery(id+"F0.wireOp",EDGE,"4bab01e7-d052-4abf-b01b-eb726d723c40.2.10"),sQuery(id+"F0.wireOp",EDGE,"4bab01e7-d052-4abf-b01b-eb726d723c40.2.11"),sQuery(id+"F0.wireOp",EDGE,"4bab01e7-d052-4abf-b01b-eb726d723c40.2.12"),sQuery(id+"F0.wireOp",EDGE,"4bab01e7-d052-4abf-b01b-eb726d723c40.2.13"),sQuery(id+"F0.wireOp",EDGE,"a3e658cf-df75-4adb-9b9d-d9da59cb78ec.3.3.0"),sQuery(id+"F0.wireOp",EDGE,"a3e658cf-df75-4adb-9b9d-d9da59cb78ec.7.3.0"),sQuery(id+"F0.wireOp",EDGE,"a3e658cf-df75-4adb-9b9d-d9da59cb78ec.8.3.0"),sQuery(id+"F0.wireOp",EDGE,"a3e658cf-df75-4adb-9b9d-d9da59cb78ec.9.3.0"),sQuery(id+"F0.wireOp",EDGE,"a3e658cf-df75-4adb-9b9d-d9da59cb78ec.17.3.0"),sQuery(id+"F0.wireOp",EDGE,"a3e658cf-df75-4adb-9b9d-d9da59cb78ec.19.3.0"),sQuery(id+"F0.wireOp",EDGE,"a3e658cf-df75-4adb-9b9d-d9da59cb78ec.23.3.0"),sQuery(id+"F0.wireOp",EDGE,"a3e658cf-df75-4adb-9b9d-d9da59cb78ec.25.3.0"),sQuery(id+"F0.wireOp",EDGE,"a3e658cf-df75-4adb-9b9d-d9da59cb78ec.27.3.0"),sQuery(id+"F0.wireOp",EDGE,"a3e658cf-df75-4adb-9b9d-d9da59cb78ec.29.3.0"),sQuery(id+"F0.wireOp",EDGE,"a3e658cf-df75-4adb-9b9d-d9da59cb78ec.3.4.0"),sQuery(id+"F0.wireOp",EDGE,"a3e658cf-df75-4adb-9b9d-d9da59cb78ec.7.4.0"),sQuery(id+"F0.wireOp",EDGE,"a3e658cf-df75-4adb-9b9d-d9da59cb78ec.8.4.0"),sQuery(id+"F0.wireOp",EDGE,"a3e658cf-df75-4adb-9b9d-d9da59cb78ec.9.4.0"),sQuery(id+"F0.wireOp",EDGE,"a3e658cf-df75-4adb-9b9d-d9da59cb78ec.17.4.0"),sQuery(id+"F0.wireOp",EDGE,"a3e658cf-df75-4adb-9b9d-d9da59cb78ec.19.4.0"),sQuery(id+"F0.wireOp",EDGE,"a3e658cf-df75-4adb-9b9d-d9da59cb78ec.23.4.0"),sQuery(id+"F0.wireOp",EDGE,"a3e658cf-df75-4adb-9b9d-d9da59cb78ec.25.4.0"),sQuery(id+"F0.wireOp",EDGE,"a3e658cf-df75-4adb-9b9d-d9da59cb78ec.27.4.0"),sQuery(id+"F0.wireOp",EDGE,"a3e658cf-df75-4adb-9b9d-d9da59cb78ec.29.4.0"),sQuery(id+"F0.wireOp",EDGE,"a3e658cf-df75-4adb-9b9d-d9da59cb78ec.3.5.0"),sQuery(id+"F0.wireOp",EDGE,"a3e658cf-df75-4adb-9b9d-d9da59cb78ec.7.5.0"),sQuery(id+"F0.wireOp",EDGE,"a3e658cf-df75-4adb-9b9d-d9da59cb78ec.8.5.0"),sQuery(id+"F0.wireOp",EDGE,"a3e658cf-df75-4adb-9b9d-d9da59cb78ec.9.5.0"),sQuery(id+"F0.wireOp",EDGE,"a3e658cf-df75-4adb-9b9d-d9da59cb78ec.17.5.0"),sQuery(id+"F0.wireOp",EDGE,"a3e658cf-df75-4adb-9b9d-d9da59cb78ec.19.5.0"),sQuery(id+"F0.wireOp",EDGE,"a3e658cf-df75-4adb-9b9d-d9da59cb78ec.23.5.0"),sQuery(id+"F0.wireOp",EDGE,"a3e658cf-df75-4adb-9b9d-d9da59cb78ec.25.5.0"),sQuery(id+"F0.wireOp",EDGE,"a3e658cf-df75-4adb-9b9d-d9da59cb78ec.27.5.0"),sQuery(id+"F0.wireOp",EDGE,"a3e658cf-df75-4adb-9b9d-d9da59cb78ec.29.5.0"),sQuery(id+"F0.wireOp",EDGE,"a3e658cf-df75-4adb-9b9d-d9da59cb78ec.3.6.0"),sQuery(id+"F0.wireOp",EDGE,"a3e658cf-df75-4adb-9b9d-d9da59cb78ec.7.6.0"),sQuery(id+"F0.wireOp",EDGE,"a3e658cf-df75-4adb-9b9d-d9da59cb78ec.8.6.0"),sQuery(id+"F0.wireOp",EDGE,"a3e658cf-df75-4adb-9b9d-d9da59cb78ec.9.6.0"),sQuery(id+"F0.wireOp",EDGE,"a3e658cf-df75-4adb-9b9d-d9da59cb78ec.17.6.0"),sQuery(id+"F0.wireOp",EDGE,"a3e658cf-df75-4adb-9b9d-d9da59cb78ec.19.6.0"),sQuery(id+"F0.wireOp",EDGE,"a3e658cf-df75-4adb-9b9d-d9da59cb78ec.23.6.0"),sQuery(id+"F0.wireOp",EDGE,"a3e658cf-df75-4adb-9b9d-d9da59cb78ec.25.6.0"),sQuery(id+"F0.wireOp",EDGE,"a3e658cf-df75-4adb-9b9d-d9da59cb78ec.27.6.0"),sQuery(id+"F0.wireOp",EDGE,"a3e658cf-df75-4adb-9b9d-d9da59cb78ec.29.6.0"),sQuery(id+"F0.wireOp",EDGE,"a3e658cf-df75-4adb-9b9d-d9da59cb78ec.3.7.0"),sQuery(id+"F0.wireOp",EDGE,"a3e658cf-df75-4adb-9b9d-d9da59cb78ec.7.7.0"),sQuery(id+"F0.wireOp",EDGE,"a3e658cf-df75-4adb-9b9d-d9da59cb78ec.8.7.0"),sQuery(id+"F0.wireOp",EDGE,"a3e658cf-df75-4adb-9b9d-d9da59cb78ec.9.7.0"),sQuery(id+"F0.wireOp",EDGE,"a3e658cf-df75-4adb-9b9d-d9da59cb78ec.17.7.0"),sQuery(id+"F0.wireOp",EDGE,"a3e658cf-df75-4adb-9b9d-d9da59cb78ec.19.7.0"),sQuery(id+"F0.wireOp",EDGE,"a3e658cf-df75-4adb-9b9d-d9da59cb78ec.23.7.0"),sQuery(id+"F0.wireOp",EDGE,"a3e658cf-df75-4adb-9b9d-d9da59cb78ec.25.7.0"),sQuery(id+"F0.wireOp",EDGE,"a3e658cf-df75-4adb-9b9d-d9da59cb78ec.27.7.0"),sQuery(id+"F0.wireOp",EDGE,"a3e658cf-df75-4adb-9b9d-d9da59cb78ec.29.7.0"),sQuery(id+"F0.wireOp",EDGE,"a3e658cf-df75-4adb-9b9d-d9da59cb78ec.3.8.0"),sQuery(id+"F0.wireOp",EDGE,"a3e658cf-df75-4adb-9b9d-d9da59cb78ec.7.8.0"),sQuery(id+"F0.wireOp",EDGE,"a3e658cf-df75-4adb-9b9d-d9da59cb78ec.8.8.0"),sQuery(id+"F0.wireOp",EDGE,"a3e658cf-df75-4adb-9b9d-d9da59cb78ec.9.8.0"),sQuery(id+"F0.wireOp",EDGE,"a3e658cf-df75-4adb-9b9d-d9da59cb78ec.17.8.0"),sQuery(id+"F0.wireOp",EDGE,"a3e658cf-df75-4adb-9b9d-d9da59cb78ec.19.8.0"),sQuery(id+"F0.wireOp",EDGE,"a3e658cf-df75-4adb-9b9d-d9da59cb78ec.23.8.0"),sQuery(id+"F0.wireOp",EDGE,"a3e658cf-df75-4adb-9b9d-d9da59cb78ec.25.8.0"),sQuery(id+"F0.wireOp",EDGE,"a3e658cf-df75-4adb-9b9d-d9da59cb78ec.27.8.0"),sQuery(id+"F0.wireOp",EDGE,"a3e658cf-df75-4adb-9b9d-d9da59cb78ec.29.8.0"),sQuery(id+"F0.wireOp",EDGE,"a3e658cf-df75-4adb-9b9d-d9da59cb78ec.3.9.0"),sQuery(id+"F0.wireOp",EDGE,"a3e658cf-df75-4adb-9b9d-d9da59cb78ec.7.9.0"),sQuery(id+"F0.wireOp",EDGE,"a3e658cf-df75-4adb-9b9d-d9da59cb78ec.8.9.0"),sQuery(id+"F0.wireOp",EDGE,"a3e658cf-df75-4adb-9b9d-d9da59cb78ec.9.9.0"),sQuery(id+"F0.wireOp",EDGE,"a3e658cf-df75-4adb-9b9d-d9da59cb78ec.17.9.0"),sQuery(id+"F0.wireOp",EDGE,"a3e658cf-df75-4adb-9b9d-d9da59cb78ec.19.9.0"),sQuery(id+"F0.wireOp",EDGE,"a3e658cf-df75-4adb-9b9d-d9da59cb78ec.23.9.0"),sQuery(id+"F0.wireOp",EDGE,"a3e658cf-df75-4adb-9b9d-d9da59cb78ec.25.9.0"),sQuery(id+"F0.wireOp",EDGE,"a3e658cf-df75-4adb-9b9d-d9da59cb78ec.27.9.0"),sQuery(id+"F0.wireOp",EDGE,"a3e658cf-df75-4adb-9b9d-d9da59cb78ec.29.9.0"),sQuery(id+"F0.wireOp",EDGE,"a3e658cf-df75-4adb-9b9d-d9da59cb78ec.3.10.0"),sQuery(id+"F0.wireOp",EDGE,"a3e658cf-df75-4adb-9b9d-d9da59cb78ec.7.10.0"),sQuery(id+"F0.wireOp",EDGE,"a3e658cf-df75-4adb-9b9d-d9da59cb78ec.8.10.0"),sQuery(id+"F0.wireOp",EDGE,"a3e658cf-df75-4adb-9b9d-d9da59cb78ec.9.10.0"),sQuery(id+"F0.wireOp",EDGE,"a3e658cf-df75-4adb-9b9d-d9da59cb78ec.17.10.0"),sQuery(id+"F0.wireOp",EDGE,"a3e658cf-df75-4adb-9b9d-d9da59cb78ec.19.10.0"),sQuery(id+"F0.wireOp",EDGE,"a3e658cf-df75-4adb-9b9d-d9da59cb78ec.23.10.0"),sQuery(id+"F0.wireOp",EDGE,"a3e658cf-df75-4adb-9b9d-d9da59cb78ec.25.10.0"),sQuery(id+"F0.wireOp",EDGE,"a3e658cf-df75-4adb-9b9d-d9da59cb78ec.27.10.0"),sQuery(id+"F0.wireOp",EDGE,"a3e658cf-df75-4adb-9b9d-d9da59cb78ec.29.10.0"),sQuery(id+"F0.wireOp",EDGE,"a3e658cf-df75-4adb-9b9d-d9da59cb78ec.3.11.0"),sQuery(id+"F0.wireOp",EDGE,"a3e658cf-df75-4adb-9b9d-d9da59cb78ec.7.11.0"),sQuery(id+"F0.wireOp",EDGE,"a3e658cf-df75-4adb-9b9d-d9da59cb78ec.8.11.0"),sQuery(id+"F0.wireOp",EDGE,"a3e658cf-df75-4adb-9b9d-d9da59cb78ec.9.11.0"),sQuery(id+"F0.wireOp",EDGE,"a3e658cf-df75-4adb-9b9d-d9da59cb78ec.17.11.0"),sQuery(id+"F0.wireOp",EDGE,"a3e658cf-df75-4adb-9b9d-d9da59cb78ec.19.11.0"),sQuery(id+"F0.wireOp",EDGE,"a3e658cf-df75-4adb-9b9d-d9da59cb78ec.23.11.0"),sQuery(id+"F0.wireOp",EDGE,"a3e658cf-df75-4adb-9b9d-d9da59cb78ec.25.11.0"),sQuery(id+"F0.wireOp",EDGE,"a3e658cf-df75-4adb-9b9d-d9da59cb78ec.27.11.0"),sQuery(id+"F0.wireOp",EDGE,"a3e658cf-df75-4adb-9b9d-d9da59cb78ec.29.11.0"),sQuery(id+"F0.wireOp",EDGE,"a3e658cf-df75-4adb-9b9d-d9da59cb78ec.3.12.0"),sQuery(id+"F0.wireOp",EDGE,"a3e658cf-df75-4adb-9b9d-d9da59cb78ec.7.12.0"),sQuery(id+"F0.wireOp",EDGE,"a3e658cf-df75-4adb-9b9d-d9da59cb78ec.8.12.0"),sQuery(id+"F0.wireOp",EDGE,"a3e658cf-df75-4adb-9b9d-d9da59cb78ec.9.12.0"),sQuery(id+"F0.wireOp",EDGE,"a3e658cf-df75-4adb-9b9d-d9da59cb78ec.17.12.0"),sQuery(id+"F0.wireOp",EDGE,"a3e658cf-df75-4adb-9b9d-d9da59cb78ec.19.12.0"),sQuery(id+"F0.wireOp",EDGE,"a3e658cf-df75-4adb-9b9d-d9da59cb78ec.23.12.0"),sQuery(id+"F0.wireOp",EDGE,"a3e658cf-df75-4adb-9b9d-d9da59cb78ec.25.12.0"),sQuery(id+"F0.wireOp",EDGE,"a3e658cf-df75-4adb-9b9d-d9da59cb78ec.27.12.0"),sQuery(id+"F0.wireOp",EDGE,"a3e658cf-df75-4adb-9b9d-d9da59cb78ec.29.12.0"),sQuery(id+"F0.wireOp",EDGE,"a3e658cf-df75-4adb-9b9d-d9da59cb78ec.3.13.0"),sQuery(id+"F0.wireOp",EDGE,"a3e658cf-df75-4adb-9b9d-d9da59cb78ec.7.13.0"),sQuery(id+"F0.wireOp",EDGE,"a3e658cf-df75-4adb-9b9d-d9da59cb78ec.8.13.0"),sQuery(id+"F0.wireOp",EDGE,"a3e658cf-df75-4adb-9b9d-d9da59cb78ec.9.13.0"),sQuery(id+"F0.wireOp",EDGE,"a3e658cf-df75-4adb-9b9d-d9da59cb78ec.17.13.0"),sQuery(id+"F0.wireOp",EDGE,"a3e658cf-df75-4adb-9b9d-d9da59cb78ec.19.13.0"),sQuery(id+"F0.wireOp",EDGE,"a3e658cf-df75-4adb-9b9d-d9da59cb78ec.23.13.0"),sQuery(id+"F0.wireOp",EDGE,"a3e658cf-df75-4adb-9b9d-d9da59cb78ec.25.13.0"),sQuery(id+"F0.wireOp",EDGE,"a3e658cf-df75-4adb-9b9d-d9da59cb78ec.27.13.0"),sQuery(id+"F0.wireOp",EDGE,"a3e658cf-df75-4adb-9b9d-d9da59cb78ec.29.13.0"),sQuery(id+"F0.wireOp",EDGE,"a3e658cf-df75-4adb-9b9d-d9da59cb78ec.3.14.0"),sQuery(id+"F0.wireOp",EDGE,"a3e658cf-df75-4adb-9b9d-d9da59cb78ec.7.14.0"),sQuery(id+"F0.wireOp",EDGE,"a3e658cf-df75-4adb-9b9d-d9da59cb78ec.8.14.0"),sQuery(id+"F0.wireOp",EDGE,"a3e658cf-df75-4adb-9b9d-d9da59cb78ec.9.14.0"),sQuery(id+"F0.wireOp",EDGE,"a3e658cf-df75-4adb-9b9d-d9da59cb78ec.17.14.0"),sQuery(id+"F0.wireOp",EDGE,"a3e658cf-df75-4adb-9b9d-d9da59cb78ec.19.14.0"),sQuery(id+"F0.wireOp",EDGE,"a3e658cf-df75-4adb-9b9d-d9da59cb78ec.23.14.0"),sQuery(id+"F0.wireOp",EDGE,"a3e658cf-df75-4adb-9b9d-d9da59cb78ec.25.14.0"),sQuery(id+"F0.wireOp",EDGE,"a3e658cf-df75-4adb-9b9d-d9da59cb78ec.27.14.0"),sQuery(id+"F0.wireOp",EDGE,"a3e658cf-df75-4adb-9b9d-d9da59cb78ec.29.14.0"),sQuery(id+"F0.wireOp",EDGE,"a3e658cf-df75-4adb-9b9d-d9da59cb78ec.3.15.0"),sQuery(id+"F0.wireOp",EDGE,"a3e658cf-df75-4adb-9b9d-d9da59cb78ec.7.15.0"),sQuery(id+"F0.wireOp",EDGE,"a3e658cf-df75-4adb-9b9d-d9da59cb78ec.8.15.0"),sQuery(id+"F0.wireOp",EDGE,"a3e658cf-df75-4adb-9b9d-d9da59cb78ec.9.15.0"),sQuery(id+"F0.wireOp",EDGE,"a3e658cf-df75-4adb-9b9d-d9da59cb78ec.17.15.0"),sQuery(id+"F0.wireOp",EDGE,"a3e658cf-df75-4adb-9b9d-d9da59cb78ec.19.15.0"),sQuery(id+"F0.wireOp",EDGE,"a3e658cf-df75-4adb-9b9d-d9da59cb78ec.23.15.0"),sQuery(id+"F0.wireOp",EDGE,"a3e658cf-df75-4adb-9b9d-d9da59cb78ec.25.15.0"),sQuery(id+"F0.wireOp",EDGE,"a3e658cf-df75-4adb-9b9d-d9da59cb78ec.27.15.0"),sQuery(id+"F0.wireOp",EDGE,"a3e658cf-df75-4adb-9b9d-d9da59cb78ec.29.15.0"),sQuery(id+"F0.wireOp",EDGE,"E1")])],"isStart":false});
            chamfer(context, id + "F2", {"entities" : qUnion([Q0]), "width" : .15 * mm, "tangentPropagation" : true});
        }
    });
